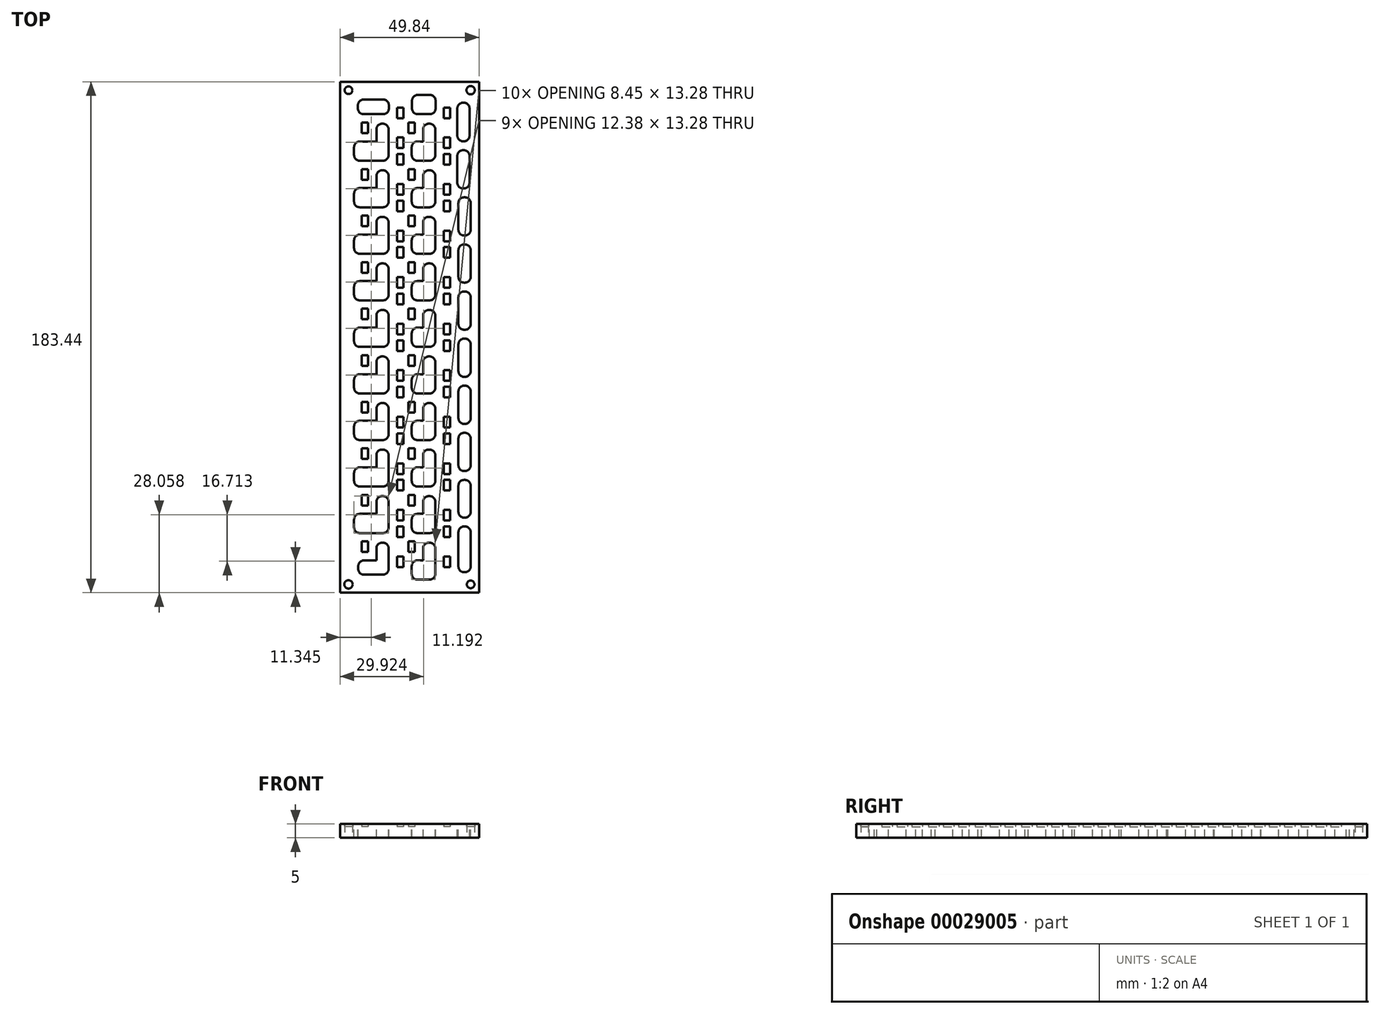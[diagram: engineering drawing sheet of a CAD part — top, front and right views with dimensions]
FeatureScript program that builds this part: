
annotation { "Feature Type Name" : "Feature", "Feature Type Description" : "" }
export const myFeature = defineFeature(function(context is Context, id is Id, definition is map)
    precondition{}
    {
        {
            var Q0;
            Q0=qCreatedBy(makeId("Top.planeOp"),FACE);
            var sketch = newSketch(context, id + "F0", { "sketchPlane" : qUnion([Q0])});
            skCircle(sketch, "E0", {"center": v(0, 0) * mm, "radius": 1.5 * mm});
            skCircle(sketch, "E1", {"center": v(43.84, 177.44) * mm, "radius": 1.5 * mm});
            skLineSegment(sketch, "E2.bottom", {"start": v(-3, 180.44) * mm, "end": v(46.84, 180.44) * mm});
            skLineSegment(sketch, "E2.top", {"start": v(-3, -3) * mm, "end": v(46.84, -3) * mm});
            skLineSegment(sketch, "E2.left", {"start": v(-3, 180.44) * mm, "end": v(-3, -3) * mm});
            skLineSegment(sketch, "E2.right", {"start": v(46.84, 180.44) * mm, "end": v(46.84, -3) * mm});
            skLineSegment(sketch, "E3.rect.bottom", {"start": v(19.7, 6.23) * mm, "end": v(17.38, 6.23) * mm});
            skLineSegment(sketch, "E3.rect.top", {"start": v(19.7, 10.04) * mm, "end": v(17.38, 10.04) * mm});
            skLineSegment(sketch, "E3.rect.left", {"start": v(19.7, 6.23) * mm, "end": v(19.7, 10.04) * mm});
            skLineSegment(sketch, "E3.rect.right", {"start": v(17.38, 6.23) * mm, "end": v(17.38, 10.04) * mm});
            skPoint(sketch, "E3.rect.middle", {"position": v(18.54, 8.14) * mm});
            skLineSegment(sketch, "E4.rect.right", {"start": v(4.72, 11.6) * mm, "end": v(4.72, 15.42) * mm});
            skLineSegment(sketch, "E4.rect.left", {"start": v(7.03, 11.6) * mm, "end": v(7.03, 15.42) * mm});
            skLineSegment(sketch, "E4.rect.top", {"start": v(7.03, 15.42) * mm, "end": v(4.72, 15.42) * mm});
            skPoint(sketch, "E4.rect.middle", {"position": v(5.88, 13.51) * mm});
            skLineSegment(sketch, "E4.rect.bottom", {"start": v(7.03, 11.6) * mm, "end": v(4.72, 11.6) * mm});
            skLineSegment(sketch, "E5.rect.top", {"start": v(19.7, 20.8) * mm, "end": v(17.38, 20.8) * mm});
            skPoint(sketch, "E5.rect.middle", {"position": v(18.54, 18.89) * mm});
            skLineSegment(sketch, "E5.rect.bottom", {"start": v(19.7, 16.98) * mm, "end": v(17.38, 16.98) * mm});
            skLineSegment(sketch, "E5.rect.left", {"start": v(19.7, 16.98) * mm, "end": v(19.7, 20.8) * mm});
            skLineSegment(sketch, "E5.rect.right", {"start": v(17.38, 16.98) * mm, "end": v(17.38, 20.8) * mm});
            skLineSegment(sketch, "E6.rect.top", {"start": v(19.7, 26.75) * mm, "end": v(17.38, 26.75) * mm});
            skLineSegment(sketch, "E7.rect.left", {"start": v(19.7, 33.7) * mm, "end": v(19.7, 37.5) * mm});
            skLineSegment(sketch, "E6.rect.bottom", {"start": v(19.7, 22.94) * mm, "end": v(17.38, 22.94) * mm});
            skPoint(sketch, "E6.rect.middle", {"position": v(18.54, 24.85) * mm});
            skLineSegment(sketch, "E8.rect.top", {"start": v(7.03, 32.13) * mm, "end": v(4.72, 32.13) * mm});
            skPoint(sketch, "E7.rect.middle", {"position": v(18.54, 35.6) * mm});
            skLineSegment(sketch, "E7.rect.bottom", {"start": v(19.7, 33.7) * mm, "end": v(17.38, 33.7) * mm});
            skLineSegment(sketch, "E7.rect.top", {"start": v(19.7, 37.5) * mm, "end": v(17.38, 37.5) * mm});
            skLineSegment(sketch, "E8.rect.bottom", {"start": v(7.03, 28.32) * mm, "end": v(4.72, 28.32) * mm});
            skLineSegment(sketch, "E7.rect.right", {"start": v(17.38, 33.7) * mm, "end": v(17.38, 37.5) * mm});
            skLineSegment(sketch, "E8.rect.left", {"start": v(7.03, 28.32) * mm, "end": v(7.03, 32.13) * mm});
            skPoint(sketch, "E8.rect.middle", {"position": v(5.88, 30.23) * mm});
            skLineSegment(sketch, "E8.rect.right", {"start": v(4.72, 28.32) * mm, "end": v(4.72, 32.13) * mm});
            skLineSegment(sketch, "E6.rect.right", {"start": v(17.38, 22.94) * mm, "end": v(17.38, 26.75) * mm});
            skLineSegment(sketch, "E6.rect.left", {"start": v(19.7, 22.94) * mm, "end": v(19.7, 26.75) * mm});
            skPoint(sketch, "E9.rect.middle", {"position": v(5.88, 46.94) * mm});
            skPoint(sketch, "E10.rect.middle", {"position": v(18.54, 52.32) * mm});
            skLineSegment(sketch, "E11.rect.left", {"start": v(19.7, 39.66) * mm, "end": v(19.7, 43.47) * mm});
            skLineSegment(sketch, "E11.rect.bottom", {"start": v(19.7, 39.66) * mm, "end": v(17.38, 39.66) * mm});
            skLineSegment(sketch, "E10.rect.top", {"start": v(19.7, 54.22) * mm, "end": v(17.38, 54.22) * mm});
            skLineSegment(sketch, "E9.rect.right", {"start": v(4.72, 45.03) * mm, "end": v(4.72, 48.84) * mm});
            skLineSegment(sketch, "E10.rect.right", {"start": v(17.38, 50.41) * mm, "end": v(17.38, 54.22) * mm});
            skLineSegment(sketch, "E9.rect.top", {"start": v(7.03, 48.84) * mm, "end": v(4.72, 48.84) * mm});
            skLineSegment(sketch, "E11.rect.right", {"start": v(17.38, 39.66) * mm, "end": v(17.38, 43.47) * mm});
            skLineSegment(sketch, "E9.rect.bottom", {"start": v(7.03, 45.03) * mm, "end": v(4.72, 45.03) * mm});
            skLineSegment(sketch, "E9.rect.left", {"start": v(7.03, 45.03) * mm, "end": v(7.03, 48.84) * mm});
            skLineSegment(sketch, "E10.rect.left", {"start": v(19.7, 50.41) * mm, "end": v(19.7, 54.22) * mm});
            skPoint(sketch, "E11.rect.middle", {"position": v(18.54, 41.56) * mm});
            skLineSegment(sketch, "E11.rect.top", {"start": v(19.7, 43.47) * mm, "end": v(17.38, 43.47) * mm});
            skLineSegment(sketch, "E10.rect.bottom", {"start": v(19.7, 50.41) * mm, "end": v(17.38, 50.41) * mm});
            skPoint(sketch, "E12.rect.middle", {"position": v(18.54, 74.99) * mm});
            skPoint(sketch, "E13.rect.middle", {"position": v(18.54, 85.74) * mm});
            skPoint(sketch, "E14.rect.middle", {"position": v(18.54, 69.03) * mm});
            skPoint(sketch, "E15.rect.middle", {"position": v(5.88, 80.37) * mm});
            skPoint(sketch, "E16.rect.middle", {"position": v(5.88, 63.65) * mm});
            skPoint(sketch, "E17.rect.middle", {"position": v(18.54, 58.28) * mm});
            skLineSegment(sketch, "E14.rect.left", {"start": v(19.7, 67.12) * mm, "end": v(19.7, 70.93) * mm});
            skLineSegment(sketch, "E12.rect.right", {"start": v(17.38, 73.08) * mm, "end": v(17.38, 76.9) * mm});
            skLineSegment(sketch, "E17.rect.left", {"start": v(19.7, 56.37) * mm, "end": v(19.7, 60.18) * mm});
            skLineSegment(sketch, "E16.rect.left", {"start": v(7.03, 61.75) * mm, "end": v(7.03, 65.56) * mm});
            skLineSegment(sketch, "E13.rect.right", {"start": v(17.38, 83.84) * mm, "end": v(17.38, 87.65) * mm});
            skLineSegment(sketch, "E15.rect.right", {"start": v(4.72, 78.46) * mm, "end": v(4.72, 82.27) * mm});
            skLineSegment(sketch, "E17.rect.right", {"start": v(17.38, 56.37) * mm, "end": v(17.38, 60.18) * mm});
            skLineSegment(sketch, "E13.rect.left", {"start": v(19.7, 83.84) * mm, "end": v(19.7, 87.65) * mm});
            skLineSegment(sketch, "E16.rect.right", {"start": v(4.72, 61.75) * mm, "end": v(4.72, 65.56) * mm});
            skLineSegment(sketch, "E15.rect.left", {"start": v(7.03, 78.46) * mm, "end": v(7.03, 82.27) * mm});
            skLineSegment(sketch, "E14.rect.right", {"start": v(17.38, 67.12) * mm, "end": v(17.38, 70.93) * mm});
            skLineSegment(sketch, "E12.rect.left", {"start": v(19.7, 73.08) * mm, "end": v(19.7, 76.9) * mm});
            skLineSegment(sketch, "E15.rect.top", {"start": v(7.03, 82.27) * mm, "end": v(4.72, 82.27) * mm});
            skLineSegment(sketch, "E17.rect.bottom", {"start": v(19.7, 56.37) * mm, "end": v(17.38, 56.37) * mm});
            skLineSegment(sketch, "E13.rect.top", {"start": v(19.7, 87.65) * mm, "end": v(17.38, 87.65) * mm});
            skLineSegment(sketch, "E17.rect.top", {"start": v(19.7, 60.18) * mm, "end": v(17.38, 60.18) * mm});
            skLineSegment(sketch, "E12.rect.bottom", {"start": v(19.7, 73.08) * mm, "end": v(17.38, 73.08) * mm});
            skLineSegment(sketch, "E13.rect.bottom", {"start": v(19.7, 83.84) * mm, "end": v(17.38, 83.84) * mm});
            skLineSegment(sketch, "E12.rect.top", {"start": v(19.7, 76.9) * mm, "end": v(17.38, 76.9) * mm});
            skLineSegment(sketch, "E14.rect.top", {"start": v(19.7, 70.93) * mm, "end": v(17.38, 70.93) * mm});
            skLineSegment(sketch, "E14.rect.bottom", {"start": v(19.7, 67.12) * mm, "end": v(17.38, 67.12) * mm});
            skLineSegment(sketch, "E15.rect.bottom", {"start": v(7.03, 78.46) * mm, "end": v(4.72, 78.46) * mm});
            skLineSegment(sketch, "E16.rect.top", {"start": v(7.03, 65.56) * mm, "end": v(4.72, 65.56) * mm});
            skLineSegment(sketch, "E16.rect.bottom", {"start": v(7.03, 61.75) * mm, "end": v(4.72, 61.75) * mm});
            skPoint(sketch, "E18.rect.middle", {"position": v(5.88, 130.5) * mm});
            skPoint(sketch, "E19.rect.middle", {"position": v(18.54, 152.6) * mm});
            skPoint(sketch, "E20.rect.middle", {"position": v(5.88, 97.08) * mm});
            skPoint(sketch, "E21.rect.middle", {"position": v(18.54, 102.46) * mm});
            skPoint(sketch, "E22.rect.middle", {"position": v(5.88, 147.22) * mm});
            skPoint(sketch, "E23.rect.middle", {"position": v(5.88, 113.8) * mm});
            skPoint(sketch, "E24.rect.middle", {"position": v(18.54, 119.17) * mm});
            skPoint(sketch, "E25.rect.middle", {"position": v(18.54, 125.13) * mm});
            skPoint(sketch, "E26.rect.middle", {"position": v(18.54, 91.7) * mm});
            skPoint(sketch, "E27.rect.middle", {"position": v(18.54, 141.84) * mm});
            skPoint(sketch, "E28.rect.middle", {"position": v(18.54, 135.88) * mm});
            skPoint(sketch, "E29.rect.middle", {"position": v(18.54, 108.42) * mm});
            skLineSegment(sketch, "E19.rect.right", {"start": v(17.38, 150.7) * mm, "end": v(17.38, 154.5) * mm});
            skLineSegment(sketch, "E23.rect.left", {"start": v(7.03, 111.89) * mm, "end": v(7.03, 115.7) * mm});
            skLineSegment(sketch, "E25.rect.left", {"start": v(19.7, 123.22) * mm, "end": v(19.7, 127.03) * mm});
            skLineSegment(sketch, "E26.rect.right", {"start": v(17.38, 89.8) * mm, "end": v(17.38, 93.6) * mm});
            skLineSegment(sketch, "E27.rect.left", {"start": v(19.7, 139.94) * mm, "end": v(19.7, 143.75) * mm});
            skLineSegment(sketch, "E18.rect.right", {"start": v(4.72, 128.6) * mm, "end": v(4.72, 132.41) * mm});
            skLineSegment(sketch, "E21.rect.right", {"start": v(17.38, 100.55) * mm, "end": v(17.38, 104.36) * mm});
            skLineSegment(sketch, "E23.rect.right", {"start": v(4.72, 111.89) * mm, "end": v(4.72, 115.7) * mm});
            skLineSegment(sketch, "E19.rect.left", {"start": v(19.7, 150.7) * mm, "end": v(19.7, 154.5) * mm});
            skLineSegment(sketch, "E25.rect.right", {"start": v(17.38, 123.22) * mm, "end": v(17.38, 127.03) * mm});
            skLineSegment(sketch, "E26.rect.left", {"start": v(19.7, 89.8) * mm, "end": v(19.7, 93.6) * mm});
            skLineSegment(sketch, "E18.rect.left", {"start": v(7.03, 128.6) * mm, "end": v(7.03, 132.41) * mm});
            skLineSegment(sketch, "E28.rect.right", {"start": v(17.38, 133.98) * mm, "end": v(17.38, 137.79) * mm});
            skLineSegment(sketch, "E20.rect.right", {"start": v(4.72, 95.17) * mm, "end": v(4.72, 98.98) * mm});
            skLineSegment(sketch, "E27.rect.right", {"start": v(17.38, 139.94) * mm, "end": v(17.38, 143.75) * mm});
            skLineSegment(sketch, "E21.rect.left", {"start": v(19.7, 100.55) * mm, "end": v(19.7, 104.36) * mm});
            skLineSegment(sketch, "E28.rect.left", {"start": v(19.7, 133.98) * mm, "end": v(19.7, 137.79) * mm});
            skLineSegment(sketch, "E20.rect.left", {"start": v(7.03, 95.17) * mm, "end": v(7.03, 98.98) * mm});
            skLineSegment(sketch, "E24.rect.left", {"start": v(19.7, 117.26) * mm, "end": v(19.7, 121.07) * mm});
            skLineSegment(sketch, "E25.rect.bottom", {"start": v(19.7, 123.22) * mm, "end": v(17.38, 123.22) * mm});
            skLineSegment(sketch, "E21.rect.top", {"start": v(19.7, 104.36) * mm, "end": v(17.38, 104.36) * mm});
            skLineSegment(sketch, "E23.rect.bottom", {"start": v(7.03, 111.89) * mm, "end": v(4.72, 111.89) * mm});
            skLineSegment(sketch, "E22.rect.right", {"start": v(4.72, 145.31) * mm, "end": v(4.72, 149.12) * mm});
            skLineSegment(sketch, "E29.rect.top", {"start": v(19.7, 110.32) * mm, "end": v(17.38, 110.32) * mm});
            skLineSegment(sketch, "E22.rect.bottom", {"start": v(7.03, 145.31) * mm, "end": v(4.72, 145.31) * mm});
            skLineSegment(sketch, "E29.rect.left", {"start": v(19.7, 106.51) * mm, "end": v(19.7, 110.32) * mm});
            skLineSegment(sketch, "E29.rect.bottom", {"start": v(19.7, 106.51) * mm, "end": v(17.38, 106.51) * mm});
            skLineSegment(sketch, "E18.rect.bottom", {"start": v(7.03, 128.6) * mm, "end": v(4.72, 128.6) * mm});
            skLineSegment(sketch, "E21.rect.bottom", {"start": v(19.7, 100.55) * mm, "end": v(17.38, 100.55) * mm});
            skLineSegment(sketch, "E20.rect.top", {"start": v(7.03, 98.98) * mm, "end": v(4.72, 98.98) * mm});
            skLineSegment(sketch, "E28.rect.bottom", {"start": v(19.7, 133.98) * mm, "end": v(17.38, 133.98) * mm});
            skLineSegment(sketch, "E24.rect.right", {"start": v(17.38, 117.26) * mm, "end": v(17.38, 121.07) * mm});
            skLineSegment(sketch, "E26.rect.top", {"start": v(19.7, 93.6) * mm, "end": v(17.38, 93.6) * mm});
            skLineSegment(sketch, "E24.rect.bottom", {"start": v(19.7, 117.26) * mm, "end": v(17.38, 117.26) * mm});
            skLineSegment(sketch, "E20.rect.bottom", {"start": v(7.03, 95.17) * mm, "end": v(4.72, 95.17) * mm});
            skLineSegment(sketch, "E19.rect.top", {"start": v(19.7, 154.5) * mm, "end": v(17.38, 154.5) * mm});
            skLineSegment(sketch, "E22.rect.top", {"start": v(7.03, 149.12) * mm, "end": v(4.72, 149.12) * mm});
            skLineSegment(sketch, "E24.rect.top", {"start": v(19.7, 121.07) * mm, "end": v(17.38, 121.07) * mm});
            skLineSegment(sketch, "E18.rect.top", {"start": v(7.03, 132.41) * mm, "end": v(4.72, 132.41) * mm});
            skLineSegment(sketch, "E28.rect.top", {"start": v(19.7, 137.79) * mm, "end": v(17.38, 137.79) * mm});
            skLineSegment(sketch, "E26.rect.bottom", {"start": v(19.7, 89.8) * mm, "end": v(17.38, 89.8) * mm});
            skLineSegment(sketch, "E19.rect.bottom", {"start": v(19.7, 150.7) * mm, "end": v(17.38, 150.7) * mm});
            skLineSegment(sketch, "E23.rect.top", {"start": v(7.03, 115.7) * mm, "end": v(4.72, 115.7) * mm});
            skLineSegment(sketch, "E22.rect.left", {"start": v(7.03, 145.31) * mm, "end": v(7.03, 149.12) * mm});
            skLineSegment(sketch, "E27.rect.bottom", {"start": v(19.7, 139.94) * mm, "end": v(17.38, 139.94) * mm});
            skLineSegment(sketch, "E27.rect.top", {"start": v(19.7, 143.75) * mm, "end": v(17.38, 143.75) * mm});
            skLineSegment(sketch, "E25.rect.top", {"start": v(19.7, 127.03) * mm, "end": v(17.38, 127.03) * mm});
            skLineSegment(sketch, "E29.rect.right", {"start": v(17.38, 106.51) * mm, "end": v(17.38, 110.32) * mm});
            skPoint(sketch, "E30.rect.middle", {"position": v(18.54, 169.3) * mm});
            skPoint(sketch, "E31.rect.middle", {"position": v(18.54, 158.56) * mm});
            skPoint(sketch, "E32.rect.middle", {"position": v(5.88, 163.93) * mm});
            skLineSegment(sketch, "E32.rect.left", {"start": v(7.03, 162.03) * mm, "end": v(7.03, 165.84) * mm});
            skLineSegment(sketch, "E31.rect.right", {"start": v(17.38, 156.65) * mm, "end": v(17.38, 160.46) * mm});
            skLineSegment(sketch, "E30.rect.right", {"start": v(17.38, 167.4) * mm, "end": v(17.38, 171.21) * mm});
            skLineSegment(sketch, "E30.rect.left", {"start": v(19.7, 167.4) * mm, "end": v(19.7, 171.21) * mm});
            skLineSegment(sketch, "E32.rect.right", {"start": v(4.72, 162.03) * mm, "end": v(4.72, 165.84) * mm});
            skLineSegment(sketch, "E31.rect.left", {"start": v(19.7, 156.65) * mm, "end": v(19.7, 160.46) * mm});
            skLineSegment(sketch, "E30.rect.bottom", {"start": v(19.7, 167.4) * mm, "end": v(17.38, 167.4) * mm});
            skLineSegment(sketch, "E31.rect.top", {"start": v(19.7, 160.46) * mm, "end": v(17.38, 160.46) * mm});
            skLineSegment(sketch, "E31.rect.bottom", {"start": v(19.7, 156.65) * mm, "end": v(17.38, 156.65) * mm});
            skLineSegment(sketch, "E32.rect.bottom", {"start": v(7.03, 162.03) * mm, "end": v(4.72, 162.03) * mm});
            skLineSegment(sketch, "E32.rect.top", {"start": v(7.03, 165.84) * mm, "end": v(4.72, 165.84) * mm});
            skLineSegment(sketch, "E30.rect.top", {"start": v(19.7, 171.21) * mm, "end": v(17.38, 171.21) * mm});
            skPoint(sketch, "E33.rect.middle", {"position": v(35.3, 135.88) * mm});
            skPoint(sketch, "E34.rect.middle", {"position": v(35.3, 74.99) * mm});
            skPoint(sketch, "E35.rect.middle", {"position": v(22.64, 63.65) * mm});
            skPoint(sketch, "E36.rect.middle", {"position": v(22.64, 97.08) * mm});
            skPoint(sketch, "E37.rect.middle", {"position": v(35.3, 8.14) * mm});
            skPoint(sketch, "E38.rect.middle", {"position": v(35.3, 35.6) * mm});
            skPoint(sketch, "E39.rect.middle", {"position": v(35.3, 108.42) * mm});
            skPoint(sketch, "E40.rect.middle", {"position": v(35.3, 58.28) * mm});
            skPoint(sketch, "E41.rect.middle", {"position": v(35.3, 158.56) * mm});
            skPoint(sketch, "E42.rect.middle", {"position": v(35.3, 24.85) * mm});
            skPoint(sketch, "E43.rect.middle", {"position": v(22.64, 130.5) * mm});
            skPoint(sketch, "E44.rect.middle", {"position": v(35.3, 18.89) * mm});
            skPoint(sketch, "E45.rect.middle", {"position": v(35.3, 102.46) * mm});
            skPoint(sketch, "E46.rect.middle", {"position": v(35.3, 125.13) * mm});
            skPoint(sketch, "E47.rect.middle", {"position": v(35.3, 91.7) * mm});
            skPoint(sketch, "E48.rect.middle", {"position": v(35.3, 41.56) * mm});
            skPoint(sketch, "E49.rect.middle", {"position": v(35.3, 141.84) * mm});
            skPoint(sketch, "E50.rect.middle", {"position": v(35.3, 85.74) * mm});
            skPoint(sketch, "E51.rect.middle", {"position": v(35.3, 69.03) * mm});
            skPoint(sketch, "E52.rect.middle", {"position": v(35.3, 169.3) * mm});
            skPoint(sketch, "E53.rect.middle", {"position": v(35.3, 152.6) * mm});
            skPoint(sketch, "E54.rect.middle", {"position": v(22.64, 163.93) * mm});
            skPoint(sketch, "E55.rect.middle", {"position": v(22.64, 13.51) * mm});
            skPoint(sketch, "E56.rect.middle", {"position": v(22.64, 113.8) * mm});
            skPoint(sketch, "E57.rect.middle", {"position": v(22.64, 147.22) * mm});
            skPoint(sketch, "E58.rect.middle", {"position": v(22.64, 80.37) * mm});
            skPoint(sketch, "E59.rect.middle", {"position": v(35.3, 119.17) * mm});
            skPoint(sketch, "E60.rect.middle", {"position": v(22.64, 30.23) * mm});
            skPoint(sketch, "E61.rect.middle", {"position": v(22.64, 46.94) * mm});
            skPoint(sketch, "E62.rect.middle", {"position": v(35.3, 52.32) * mm});
            skLineSegment(sketch, "E52.rect.top", {"start": v(36.46, 171.21) * mm, "end": v(34.15, 171.21) * mm});
            skLineSegment(sketch, "E37.rect.bottom", {"start": v(36.46, 6.23) * mm, "end": v(34.15, 6.23) * mm});
            skLineSegment(sketch, "E47.rect.top", {"start": v(36.46, 93.6) * mm, "end": v(34.15, 93.6) * mm});
            skLineSegment(sketch, "E57.rect.bottom", {"start": v(23.8, 145.31) * mm, "end": v(21.48, 145.31) * mm});
            skLineSegment(sketch, "E35.rect.left", {"start": v(23.8, 61.75) * mm, "end": v(23.8, 65.56) * mm});
            skLineSegment(sketch, "E53.rect.bottom", {"start": v(36.46, 150.7) * mm, "end": v(34.15, 150.7) * mm});
            skLineSegment(sketch, "E52.rect.left", {"start": v(36.46, 167.4) * mm, "end": v(36.46, 171.21) * mm});
            skLineSegment(sketch, "E34.rect.left", {"start": v(36.46, 73.08) * mm, "end": v(36.46, 76.9) * mm});
            skLineSegment(sketch, "E34.rect.top", {"start": v(36.46, 76.9) * mm, "end": v(34.15, 76.9) * mm});
            skLineSegment(sketch, "E45.rect.bottom", {"start": v(36.46, 100.55) * mm, "end": v(34.15, 100.55) * mm});
            skLineSegment(sketch, "E52.rect.bottom", {"start": v(36.46, 167.4) * mm, "end": v(34.15, 167.4) * mm});
            skLineSegment(sketch, "E48.rect.top", {"start": v(36.46, 43.47) * mm, "end": v(34.15, 43.47) * mm});
            skLineSegment(sketch, "E43.rect.bottom", {"start": v(23.8, 128.6) * mm, "end": v(21.48, 128.6) * mm});
            skLineSegment(sketch, "E47.rect.right", {"start": v(34.15, 89.8) * mm, "end": v(34.15, 93.6) * mm});
            skLineSegment(sketch, "E58.rect.top", {"start": v(23.8, 82.27) * mm, "end": v(21.48, 82.27) * mm});
            skLineSegment(sketch, "E34.rect.right", {"start": v(34.15, 73.08) * mm, "end": v(34.15, 76.9) * mm});
            skLineSegment(sketch, "E50.rect.bottom", {"start": v(36.46, 83.84) * mm, "end": v(34.15, 83.84) * mm});
            skLineSegment(sketch, "E38.rect.bottom", {"start": v(36.46, 33.7) * mm, "end": v(34.15, 33.7) * mm});
            skLineSegment(sketch, "E44.rect.bottom", {"start": v(36.46, 16.98) * mm, "end": v(34.15, 16.98) * mm});
            skLineSegment(sketch, "E55.rect.bottom", {"start": v(23.8, 11.6) * mm, "end": v(21.48, 11.6) * mm});
            skLineSegment(sketch, "E36.rect.top", {"start": v(23.8, 98.98) * mm, "end": v(21.48, 98.98) * mm});
            skLineSegment(sketch, "E49.rect.top", {"start": v(36.46, 143.75) * mm, "end": v(34.15, 143.75) * mm});
            skLineSegment(sketch, "E39.rect.top", {"start": v(36.46, 110.32) * mm, "end": v(34.15, 110.32) * mm});
            skLineSegment(sketch, "E41.rect.top", {"start": v(36.46, 160.46) * mm, "end": v(34.15, 160.46) * mm});
            skLineSegment(sketch, "E62.rect.bottom", {"start": v(36.46, 50.41) * mm, "end": v(34.15, 50.41) * mm});
            skLineSegment(sketch, "E40.rect.top", {"start": v(36.46, 60.18) * mm, "end": v(34.15, 60.18) * mm});
            skLineSegment(sketch, "E51.rect.bottom", {"start": v(36.46, 67.12) * mm, "end": v(34.15, 67.12) * mm});
            skLineSegment(sketch, "E33.rect.right", {"start": v(34.15, 133.98) * mm, "end": v(34.15, 137.79) * mm});
            skLineSegment(sketch, "E47.rect.left", {"start": v(36.46, 89.8) * mm, "end": v(36.46, 93.6) * mm});
            skLineSegment(sketch, "E37.rect.top", {"start": v(36.46, 10.04) * mm, "end": v(34.15, 10.04) * mm});
            skLineSegment(sketch, "E37.rect.left", {"start": v(36.46, 6.23) * mm, "end": v(36.46, 10.04) * mm});
            skLineSegment(sketch, "E37.rect.right", {"start": v(34.15, 6.23) * mm, "end": v(34.15, 10.04) * mm});
            skLineSegment(sketch, "E46.rect.top", {"start": v(36.46, 127.03) * mm, "end": v(34.15, 127.03) * mm});
            skLineSegment(sketch, "E33.rect.bottom", {"start": v(36.46, 133.98) * mm, "end": v(34.15, 133.98) * mm});
            skLineSegment(sketch, "E44.rect.left", {"start": v(36.46, 16.98) * mm, "end": v(36.46, 20.8) * mm});
            skLineSegment(sketch, "E35.rect.top", {"start": v(23.8, 65.56) * mm, "end": v(21.48, 65.56) * mm});
            skLineSegment(sketch, "E44.rect.right", {"start": v(34.15, 16.98) * mm, "end": v(34.15, 20.8) * mm});
            skLineSegment(sketch, "E35.rect.bottom", {"start": v(23.8, 61.75) * mm, "end": v(21.48, 61.75) * mm});
            skLineSegment(sketch, "E42.rect.top", {"start": v(36.46, 26.75) * mm, "end": v(34.15, 26.75) * mm});
            skLineSegment(sketch, "E33.rect.left", {"start": v(36.46, 133.98) * mm, "end": v(36.46, 137.79) * mm});
            skLineSegment(sketch, "E35.rect.right", {"start": v(21.48, 61.75) * mm, "end": v(21.48, 65.56) * mm});
            skLineSegment(sketch, "E52.rect.right", {"start": v(34.15, 167.4) * mm, "end": v(34.15, 171.21) * mm});
            skLineSegment(sketch, "E62.rect.left", {"start": v(36.46, 50.41) * mm, "end": v(36.46, 54.22) * mm});
            skLineSegment(sketch, "E38.rect.top", {"start": v(36.46, 37.5) * mm, "end": v(34.15, 37.5) * mm});
            skLineSegment(sketch, "E41.rect.left", {"start": v(36.46, 156.65) * mm, "end": v(36.46, 160.46) * mm});
            skLineSegment(sketch, "E51.rect.top", {"start": v(36.46, 70.93) * mm, "end": v(34.15, 70.93) * mm});
            skLineSegment(sketch, "E59.rect.top", {"start": v(36.46, 121.07) * mm, "end": v(34.15, 121.07) * mm});
            skLineSegment(sketch, "E40.rect.bottom", {"start": v(36.46, 56.37) * mm, "end": v(34.15, 56.37) * mm});
            skLineSegment(sketch, "E43.rect.right", {"start": v(21.48, 128.6) * mm, "end": v(21.48, 132.41) * mm});
            skLineSegment(sketch, "E56.rect.bottom", {"start": v(23.8, 111.89) * mm, "end": v(21.48, 111.89) * mm});
            skLineSegment(sketch, "E53.rect.left", {"start": v(36.46, 150.7) * mm, "end": v(36.46, 154.5) * mm});
            skLineSegment(sketch, "E39.rect.left", {"start": v(36.46, 106.51) * mm, "end": v(36.46, 110.32) * mm});
            skLineSegment(sketch, "E47.rect.bottom", {"start": v(36.46, 89.8) * mm, "end": v(34.15, 89.8) * mm});
            skLineSegment(sketch, "E46.rect.right", {"start": v(34.15, 123.22) * mm, "end": v(34.15, 127.03) * mm});
            skLineSegment(sketch, "E41.rect.bottom", {"start": v(36.46, 156.65) * mm, "end": v(34.15, 156.65) * mm});
            skLineSegment(sketch, "E43.rect.left", {"start": v(23.8, 128.6) * mm, "end": v(23.8, 132.41) * mm});
            skLineSegment(sketch, "E57.rect.right", {"start": v(21.48, 145.31) * mm, "end": v(21.48, 149.12) * mm});
            skLineSegment(sketch, "E53.rect.top", {"start": v(36.46, 154.5) * mm, "end": v(34.15, 154.5) * mm});
            skLineSegment(sketch, "E56.rect.top", {"start": v(23.8, 115.7) * mm, "end": v(21.48, 115.7) * mm});
            skLineSegment(sketch, "E61.rect.bottom", {"start": v(23.8, 45.03) * mm, "end": v(21.48, 45.03) * mm});
            skLineSegment(sketch, "E40.rect.left", {"start": v(36.46, 56.37) * mm, "end": v(36.46, 60.18) * mm});
            skLineSegment(sketch, "E50.rect.top", {"start": v(36.46, 87.65) * mm, "end": v(34.15, 87.65) * mm});
            skLineSegment(sketch, "E46.rect.bottom", {"start": v(36.46, 123.22) * mm, "end": v(34.15, 123.22) * mm});
            skLineSegment(sketch, "E43.rect.top", {"start": v(23.8, 132.41) * mm, "end": v(21.48, 132.41) * mm});
            skLineSegment(sketch, "E57.rect.left", {"start": v(23.8, 145.31) * mm, "end": v(23.8, 149.12) * mm});
            skLineSegment(sketch, "E57.rect.top", {"start": v(23.8, 149.12) * mm, "end": v(21.48, 149.12) * mm});
            skLineSegment(sketch, "E61.rect.left", {"start": v(23.8, 45.03) * mm, "end": v(23.8, 48.84) * mm});
            skLineSegment(sketch, "E45.rect.top", {"start": v(36.46, 104.36) * mm, "end": v(34.15, 104.36) * mm});
            skLineSegment(sketch, "E51.rect.left", {"start": v(36.46, 67.12) * mm, "end": v(36.46, 70.93) * mm});
            skLineSegment(sketch, "E34.rect.bottom", {"start": v(36.46, 73.08) * mm, "end": v(34.15, 73.08) * mm});
            skLineSegment(sketch, "E48.rect.bottom", {"start": v(36.46, 39.66) * mm, "end": v(34.15, 39.66) * mm});
            skLineSegment(sketch, "E36.rect.right", {"start": v(21.48, 95.17) * mm, "end": v(21.48, 98.98) * mm});
            skLineSegment(sketch, "E56.rect.right", {"start": v(21.48, 111.89) * mm, "end": v(21.48, 115.7) * mm});
            skLineSegment(sketch, "E38.rect.right", {"start": v(34.15, 33.7) * mm, "end": v(34.15, 37.5) * mm});
            skLineSegment(sketch, "E48.rect.left", {"start": v(36.46, 39.66) * mm, "end": v(36.46, 43.47) * mm});
            skLineSegment(sketch, "E50.rect.right", {"start": v(34.15, 83.84) * mm, "end": v(34.15, 87.65) * mm});
            skLineSegment(sketch, "E45.rect.right", {"start": v(34.15, 100.55) * mm, "end": v(34.15, 104.36) * mm});
            skLineSegment(sketch, "E39.rect.bottom", {"start": v(36.46, 106.51) * mm, "end": v(34.15, 106.51) * mm});
            skLineSegment(sketch, "E55.rect.right", {"start": v(21.48, 11.6) * mm, "end": v(21.48, 15.42) * mm});
            skLineSegment(sketch, "E55.rect.left", {"start": v(23.8, 11.6) * mm, "end": v(23.8, 15.42) * mm});
            skLineSegment(sketch, "E55.rect.top", {"start": v(23.8, 15.42) * mm, "end": v(21.48, 15.42) * mm});
            skLineSegment(sketch, "E40.rect.right", {"start": v(34.15, 56.37) * mm, "end": v(34.15, 60.18) * mm});
            skLineSegment(sketch, "E62.rect.top", {"start": v(36.46, 54.22) * mm, "end": v(34.15, 54.22) * mm});
            skLineSegment(sketch, "E45.rect.left", {"start": v(36.46, 100.55) * mm, "end": v(36.46, 104.36) * mm});
            skLineSegment(sketch, "E50.rect.left", {"start": v(36.46, 83.84) * mm, "end": v(36.46, 87.65) * mm});
            skLineSegment(sketch, "E61.rect.right", {"start": v(21.48, 45.03) * mm, "end": v(21.48, 48.84) * mm});
            skLineSegment(sketch, "E39.rect.right", {"start": v(34.15, 106.51) * mm, "end": v(34.15, 110.32) * mm});
            skLineSegment(sketch, "E59.rect.right", {"start": v(34.15, 117.26) * mm, "end": v(34.15, 121.07) * mm});
            skLineSegment(sketch, "E53.rect.right", {"start": v(34.15, 150.7) * mm, "end": v(34.15, 154.5) * mm});
            skLineSegment(sketch, "E38.rect.left", {"start": v(36.46, 33.7) * mm, "end": v(36.46, 37.5) * mm});
            skLineSegment(sketch, "E36.rect.left", {"start": v(23.8, 95.17) * mm, "end": v(23.8, 98.98) * mm});
            skLineSegment(sketch, "E56.rect.left", {"start": v(23.8, 111.89) * mm, "end": v(23.8, 115.7) * mm});
            skLineSegment(sketch, "E61.rect.top", {"start": v(23.8, 48.84) * mm, "end": v(21.48, 48.84) * mm});
            skLineSegment(sketch, "E41.rect.right", {"start": v(34.15, 156.65) * mm, "end": v(34.15, 160.46) * mm});
            skLineSegment(sketch, "E59.rect.bottom", {"start": v(36.46, 117.26) * mm, "end": v(34.15, 117.26) * mm});
            skLineSegment(sketch, "E59.rect.left", {"start": v(36.46, 117.26) * mm, "end": v(36.46, 121.07) * mm});
            skLineSegment(sketch, "E46.rect.left", {"start": v(36.46, 123.22) * mm, "end": v(36.46, 127.03) * mm});
            skLineSegment(sketch, "E51.rect.right", {"start": v(34.15, 67.12) * mm, "end": v(34.15, 70.93) * mm});
            skLineSegment(sketch, "E48.rect.right", {"start": v(34.15, 39.66) * mm, "end": v(34.15, 43.47) * mm});
            skLineSegment(sketch, "E36.rect.bottom", {"start": v(23.8, 95.17) * mm, "end": v(21.48, 95.17) * mm});
            skLineSegment(sketch, "E60.rect.top", {"start": v(23.8, 32.13) * mm, "end": v(21.48, 32.13) * mm});
            skLineSegment(sketch, "E62.rect.right", {"start": v(34.15, 50.41) * mm, "end": v(34.15, 54.22) * mm});
            skLineSegment(sketch, "E42.rect.left", {"start": v(36.46, 22.94) * mm, "end": v(36.46, 26.75) * mm});
            skLineSegment(sketch, "E54.rect.bottom", {"start": v(23.8, 162.03) * mm, "end": v(21.48, 162.03) * mm});
            skLineSegment(sketch, "E60.rect.left", {"start": v(23.8, 28.32) * mm, "end": v(23.8, 32.13) * mm});
            skLineSegment(sketch, "E54.rect.top", {"start": v(23.8, 165.84) * mm, "end": v(21.48, 165.84) * mm});
            skLineSegment(sketch, "E60.rect.bottom", {"start": v(23.8, 28.32) * mm, "end": v(21.48, 28.32) * mm});
            skLineSegment(sketch, "E42.rect.right", {"start": v(34.15, 22.94) * mm, "end": v(34.15, 26.75) * mm});
            skLineSegment(sketch, "E60.rect.right", {"start": v(21.48, 28.32) * mm, "end": v(21.48, 32.13) * mm});
            skLineSegment(sketch, "E54.rect.right", {"start": v(21.48, 162.03) * mm, "end": v(21.48, 165.84) * mm});
            skLineSegment(sketch, "E49.rect.left", {"start": v(36.46, 139.94) * mm, "end": v(36.46, 143.75) * mm});
            skLineSegment(sketch, "E44.rect.top", {"start": v(36.46, 20.8) * mm, "end": v(34.15, 20.8) * mm});
            skLineSegment(sketch, "E58.rect.right", {"start": v(21.48, 78.46) * mm, "end": v(21.48, 82.27) * mm});
            skLineSegment(sketch, "E58.rect.bottom", {"start": v(23.8, 78.46) * mm, "end": v(21.48, 78.46) * mm});
            skLineSegment(sketch, "E33.rect.top", {"start": v(36.46, 137.79) * mm, "end": v(34.15, 137.79) * mm});
            skLineSegment(sketch, "E49.rect.bottom", {"start": v(36.46, 139.94) * mm, "end": v(34.15, 139.94) * mm});
            skLineSegment(sketch, "E49.rect.right", {"start": v(34.15, 139.94) * mm, "end": v(34.15, 143.75) * mm});
            skLineSegment(sketch, "E58.rect.left", {"start": v(23.8, 78.46) * mm, "end": v(23.8, 82.27) * mm});
            skLineSegment(sketch, "E54.rect.left", {"start": v(23.8, 162.03) * mm, "end": v(23.8, 165.84) * mm});
            skLineSegment(sketch, "E42.rect.bottom", {"start": v(36.46, 22.94) * mm, "end": v(34.15, 22.94) * mm});
            skCircle(sketch, "E63", {"center": v(0, 177.44) * mm, "radius": 1.38 * mm});
            skCircle(sketch, "E64", {"center": v(43.84, 0) * mm, "radius": 1.38 * mm});
            skSolve(sketch);
        }
        {
            var Q0;
            Q0=makeQuery(id+"F0.imprint","IMPRINT",FACE,{"disambiguationData":[TD([[makeQuery(id+"F0.imprint","IMPRINT",EDGE,{"derivedFrom":sQuery(id+"F0.wireOp",EDGE,"E0")}),-1.0]])]});
            extrude(context, id + "F1", {"entities" : qUnion([Q0]), "depth" : 1 * mm});
        }
        {
            var Q0;
            Q0=makeQuery(id+"F1.opExtrude","CAP_FACE",FACE,{"disambiguationData":[OSD([sQuery(id+"F0.wireOp",EDGE,"E0"),sQuery(id+"F0.wireOp",EDGE,"E1"),sQuery(id+"F0.wireOp",EDGE,"E2.bottom"),sQuery(id+"F0.wireOp",EDGE,"E2.top"),sQuery(id+"F0.wireOp",EDGE,"E2.left"),sQuery(id+"F0.wireOp",EDGE,"E2.right"),sQuery(id+"F0.wireOp",EDGE,"E3.rect.bottom"),sQuery(id+"F0.wireOp",EDGE,"E3.rect.top"),sQuery(id+"F0.wireOp",EDGE,"E3.rect.left"),sQuery(id+"F0.wireOp",EDGE,"E3.rect.right"),sQuery(id+"F0.wireOp",EDGE,"E4.rect.right"),sQuery(id+"F0.wireOp",EDGE,"E4.rect.left"),sQuery(id+"F0.wireOp",EDGE,"E4.rect.top"),sQuery(id+"F0.wireOp",EDGE,"E4.rect.bottom"),sQuery(id+"F0.wireOp",EDGE,"E5.rect.top"),sQuery(id+"F0.wireOp",EDGE,"E5.rect.bottom"),sQuery(id+"F0.wireOp",EDGE,"E5.rect.left"),sQuery(id+"F0.wireOp",EDGE,"E5.rect.right"),sQuery(id+"F0.wireOp",EDGE,"E6.rect.top"),sQuery(id+"F0.wireOp",EDGE,"E7.rect.left"),sQuery(id+"F0.wireOp",EDGE,"E6.rect.bottom"),sQuery(id+"F0.wireOp",EDGE,"E8.rect.top"),sQuery(id+"F0.wireOp",EDGE,"E7.rect.bottom"),sQuery(id+"F0.wireOp",EDGE,"E7.rect.top"),sQuery(id+"F0.wireOp",EDGE,"E8.rect.bottom"),sQuery(id+"F0.wireOp",EDGE,"E7.rect.right"),sQuery(id+"F0.wireOp",EDGE,"E8.rect.left"),sQuery(id+"F0.wireOp",EDGE,"E8.rect.right"),sQuery(id+"F0.wireOp",EDGE,"E6.rect.right"),sQuery(id+"F0.wireOp",EDGE,"E6.rect.left"),sQuery(id+"F0.wireOp",EDGE,"E11.rect.left"),sQuery(id+"F0.wireOp",EDGE,"E11.rect.bottom"),sQuery(id+"F0.wireOp",EDGE,"E10.rect.top"),sQuery(id+"F0.wireOp",EDGE,"E9.rect.right"),sQuery(id+"F0.wireOp",EDGE,"E10.rect.right"),sQuery(id+"F0.wireOp",EDGE,"E9.rect.top"),sQuery(id+"F0.wireOp",EDGE,"E11.rect.right"),sQuery(id+"F0.wireOp",EDGE,"E9.rect.bottom"),sQuery(id+"F0.wireOp",EDGE,"E9.rect.left"),sQuery(id+"F0.wireOp",EDGE,"E10.rect.left"),sQuery(id+"F0.wireOp",EDGE,"E11.rect.top"),sQuery(id+"F0.wireOp",EDGE,"E10.rect.bottom"),sQuery(id+"F0.wireOp",EDGE,"E14.rect.left"),sQuery(id+"F0.wireOp",EDGE,"E12.rect.right"),sQuery(id+"F0.wireOp",EDGE,"E17.rect.left"),sQuery(id+"F0.wireOp",EDGE,"E16.rect.left"),sQuery(id+"F0.wireOp",EDGE,"E13.rect.right"),sQuery(id+"F0.wireOp",EDGE,"E15.rect.right"),sQuery(id+"F0.wireOp",EDGE,"E17.rect.right"),sQuery(id+"F0.wireOp",EDGE,"E13.rect.left"),sQuery(id+"F0.wireOp",EDGE,"E16.rect.right"),sQuery(id+"F0.wireOp",EDGE,"E15.rect.left"),sQuery(id+"F0.wireOp",EDGE,"E14.rect.right"),sQuery(id+"F0.wireOp",EDGE,"E12.rect.left"),sQuery(id+"F0.wireOp",EDGE,"E15.rect.top"),sQuery(id+"F0.wireOp",EDGE,"E17.rect.bottom"),sQuery(id+"F0.wireOp",EDGE,"E13.rect.top"),sQuery(id+"F0.wireOp",EDGE,"E17.rect.top"),sQuery(id+"F0.wireOp",EDGE,"E12.rect.bottom"),sQuery(id+"F0.wireOp",EDGE,"E13.rect.bottom"),sQuery(id+"F0.wireOp",EDGE,"E12.rect.top"),sQuery(id+"F0.wireOp",EDGE,"E14.rect.top"),sQuery(id+"F0.wireOp",EDGE,"E14.rect.bottom"),sQuery(id+"F0.wireOp",EDGE,"E15.rect.bottom"),sQuery(id+"F0.wireOp",EDGE,"E16.rect.top"),sQuery(id+"F0.wireOp",EDGE,"E16.rect.bottom"),sQuery(id+"F0.wireOp",EDGE,"E19.rect.right"),sQuery(id+"F0.wireOp",EDGE,"E23.rect.left"),sQuery(id+"F0.wireOp",EDGE,"E25.rect.left"),sQuery(id+"F0.wireOp",EDGE,"E26.rect.right"),sQuery(id+"F0.wireOp",EDGE,"E27.rect.left"),sQuery(id+"F0.wireOp",EDGE,"E18.rect.right"),sQuery(id+"F0.wireOp",EDGE,"E21.rect.right"),sQuery(id+"F0.wireOp",EDGE,"E23.rect.right"),sQuery(id+"F0.wireOp",EDGE,"E19.rect.left"),sQuery(id+"F0.wireOp",EDGE,"E25.rect.right"),sQuery(id+"F0.wireOp",EDGE,"E26.rect.left"),sQuery(id+"F0.wireOp",EDGE,"E18.rect.left"),sQuery(id+"F0.wireOp",EDGE,"E28.rect.right"),sQuery(id+"F0.wireOp",EDGE,"E20.rect.right"),sQuery(id+"F0.wireOp",EDGE,"E27.rect.right"),sQuery(id+"F0.wireOp",EDGE,"E21.rect.left"),sQuery(id+"F0.wireOp",EDGE,"E28.rect.left"),sQuery(id+"F0.wireOp",EDGE,"E20.rect.left"),sQuery(id+"F0.wireOp",EDGE,"E24.rect.left"),sQuery(id+"F0.wireOp",EDGE,"E25.rect.bottom"),sQuery(id+"F0.wireOp",EDGE,"E21.rect.top"),sQuery(id+"F0.wireOp",EDGE,"E23.rect.bottom"),sQuery(id+"F0.wireOp",EDGE,"E22.rect.right"),sQuery(id+"F0.wireOp",EDGE,"E29.rect.top"),sQuery(id+"F0.wireOp",EDGE,"E22.rect.bottom"),sQuery(id+"F0.wireOp",EDGE,"E29.rect.left"),sQuery(id+"F0.wireOp",EDGE,"E29.rect.bottom"),sQuery(id+"F0.wireOp",EDGE,"E18.rect.bottom"),sQuery(id+"F0.wireOp",EDGE,"E21.rect.bottom"),sQuery(id+"F0.wireOp",EDGE,"E20.rect.top"),sQuery(id+"F0.wireOp",EDGE,"E28.rect.bottom"),sQuery(id+"F0.wireOp",EDGE,"E24.rect.right"),sQuery(id+"F0.wireOp",EDGE,"E26.rect.top"),sQuery(id+"F0.wireOp",EDGE,"E24.rect.bottom"),sQuery(id+"F0.wireOp",EDGE,"E20.rect.bottom"),sQuery(id+"F0.wireOp",EDGE,"E19.rect.top"),sQuery(id+"F0.wireOp",EDGE,"E22.rect.top"),sQuery(id+"F0.wireOp",EDGE,"E24.rect.top"),sQuery(id+"F0.wireOp",EDGE,"E18.rect.top"),sQuery(id+"F0.wireOp",EDGE,"E28.rect.top"),sQuery(id+"F0.wireOp",EDGE,"E26.rect.bottom"),sQuery(id+"F0.wireOp",EDGE,"E19.rect.bottom"),sQuery(id+"F0.wireOp",EDGE,"E23.rect.top"),sQuery(id+"F0.wireOp",EDGE,"E22.rect.left"),sQuery(id+"F0.wireOp",EDGE,"E27.rect.bottom"),sQuery(id+"F0.wireOp",EDGE,"E27.rect.top"),sQuery(id+"F0.wireOp",EDGE,"E25.rect.top"),sQuery(id+"F0.wireOp",EDGE,"E29.rect.right"),sQuery(id+"F0.wireOp",EDGE,"E32.rect.left"),sQuery(id+"F0.wireOp",EDGE,"E31.rect.right"),sQuery(id+"F0.wireOp",EDGE,"E30.rect.right"),sQuery(id+"F0.wireOp",EDGE,"E30.rect.left"),sQuery(id+"F0.wireOp",EDGE,"E32.rect.right"),sQuery(id+"F0.wireOp",EDGE,"E31.rect.left"),sQuery(id+"F0.wireOp",EDGE,"E30.rect.bottom"),sQuery(id+"F0.wireOp",EDGE,"E31.rect.top"),sQuery(id+"F0.wireOp",EDGE,"E31.rect.bottom"),sQuery(id+"F0.wireOp",EDGE,"E32.rect.bottom"),sQuery(id+"F0.wireOp",EDGE,"E32.rect.top"),sQuery(id+"F0.wireOp",EDGE,"E30.rect.top"),sQuery(id+"F0.wireOp",EDGE,"E52.rect.top"),sQuery(id+"F0.wireOp",EDGE,"E37.rect.bottom"),sQuery(id+"F0.wireOp",EDGE,"E47.rect.top"),sQuery(id+"F0.wireOp",EDGE,"E57.rect.bottom"),sQuery(id+"F0.wireOp",EDGE,"E35.rect.left"),sQuery(id+"F0.wireOp",EDGE,"E53.rect.bottom"),sQuery(id+"F0.wireOp",EDGE,"E52.rect.left"),sQuery(id+"F0.wireOp",EDGE,"E34.rect.left"),sQuery(id+"F0.wireOp",EDGE,"E34.rect.top"),sQuery(id+"F0.wireOp",EDGE,"E45.rect.bottom"),sQuery(id+"F0.wireOp",EDGE,"E52.rect.bottom"),sQuery(id+"F0.wireOp",EDGE,"E48.rect.top"),sQuery(id+"F0.wireOp",EDGE,"E43.rect.bottom"),sQuery(id+"F0.wireOp",EDGE,"E47.rect.right"),sQuery(id+"F0.wireOp",EDGE,"E58.rect.top"),sQuery(id+"F0.wireOp",EDGE,"E34.rect.right"),sQuery(id+"F0.wireOp",EDGE,"E50.rect.bottom"),sQuery(id+"F0.wireOp",EDGE,"E38.rect.bottom"),sQuery(id+"F0.wireOp",EDGE,"E44.rect.bottom"),sQuery(id+"F0.wireOp",EDGE,"E55.rect.bottom"),sQuery(id+"F0.wireOp",EDGE,"E36.rect.top"),sQuery(id+"F0.wireOp",EDGE,"E49.rect.top"),sQuery(id+"F0.wireOp",EDGE,"E39.rect.top"),sQuery(id+"F0.wireOp",EDGE,"E41.rect.top"),sQuery(id+"F0.wireOp",EDGE,"E62.rect.bottom"),sQuery(id+"F0.wireOp",EDGE,"E40.rect.top"),sQuery(id+"F0.wireOp",EDGE,"E51.rect.bottom"),sQuery(id+"F0.wireOp",EDGE,"E33.rect.right"),sQuery(id+"F0.wireOp",EDGE,"E47.rect.left"),sQuery(id+"F0.wireOp",EDGE,"E37.rect.top"),sQuery(id+"F0.wireOp",EDGE,"E37.rect.left"),sQuery(id+"F0.wireOp",EDGE,"E37.rect.right"),sQuery(id+"F0.wireOp",EDGE,"E46.rect.top"),sQuery(id+"F0.wireOp",EDGE,"E33.rect.bottom"),sQuery(id+"F0.wireOp",EDGE,"E44.rect.left"),sQuery(id+"F0.wireOp",EDGE,"E35.rect.top"),sQuery(id+"F0.wireOp",EDGE,"E44.rect.right"),sQuery(id+"F0.wireOp",EDGE,"E35.rect.bottom"),sQuery(id+"F0.wireOp",EDGE,"E42.rect.top"),sQuery(id+"F0.wireOp",EDGE,"E33.rect.left"),sQuery(id+"F0.wireOp",EDGE,"E35.rect.right"),sQuery(id+"F0.wireOp",EDGE,"E52.rect.right"),sQuery(id+"F0.wireOp",EDGE,"E62.rect.left"),sQuery(id+"F0.wireOp",EDGE,"E38.rect.top"),sQuery(id+"F0.wireOp",EDGE,"E41.rect.left"),sQuery(id+"F0.wireOp",EDGE,"E51.rect.top"),sQuery(id+"F0.wireOp",EDGE,"E59.rect.top"),sQuery(id+"F0.wireOp",EDGE,"E40.rect.bottom"),sQuery(id+"F0.wireOp",EDGE,"E43.rect.right"),sQuery(id+"F0.wireOp",EDGE,"E56.rect.bottom"),sQuery(id+"F0.wireOp",EDGE,"E53.rect.left"),sQuery(id+"F0.wireOp",EDGE,"E39.rect.left"),sQuery(id+"F0.wireOp",EDGE,"E47.rect.bottom"),sQuery(id+"F0.wireOp",EDGE,"E46.rect.right"),sQuery(id+"F0.wireOp",EDGE,"E41.rect.bottom"),sQuery(id+"F0.wireOp",EDGE,"E43.rect.left"),sQuery(id+"F0.wireOp",EDGE,"E57.rect.right"),sQuery(id+"F0.wireOp",EDGE,"E53.rect.top"),sQuery(id+"F0.wireOp",EDGE,"E56.rect.top"),sQuery(id+"F0.wireOp",EDGE,"E61.rect.bottom"),sQuery(id+"F0.wireOp",EDGE,"E40.rect.left"),sQuery(id+"F0.wireOp",EDGE,"E50.rect.top"),sQuery(id+"F0.wireOp",EDGE,"E46.rect.bottom"),sQuery(id+"F0.wireOp",EDGE,"E43.rect.top"),sQuery(id+"F0.wireOp",EDGE,"E57.rect.left"),sQuery(id+"F0.wireOp",EDGE,"E57.rect.top"),sQuery(id+"F0.wireOp",EDGE,"E61.rect.left"),sQuery(id+"F0.wireOp",EDGE,"E45.rect.top"),sQuery(id+"F0.wireOp",EDGE,"E51.rect.left"),sQuery(id+"F0.wireOp",EDGE,"E34.rect.bottom"),sQuery(id+"F0.wireOp",EDGE,"E48.rect.bottom"),sQuery(id+"F0.wireOp",EDGE,"E36.rect.right"),sQuery(id+"F0.wireOp",EDGE,"E56.rect.right"),sQuery(id+"F0.wireOp",EDGE,"E38.rect.right"),sQuery(id+"F0.wireOp",EDGE,"E48.rect.left"),sQuery(id+"F0.wireOp",EDGE,"E50.rect.right"),sQuery(id+"F0.wireOp",EDGE,"E45.rect.right"),sQuery(id+"F0.wireOp",EDGE,"E39.rect.bottom"),sQuery(id+"F0.wireOp",EDGE,"E55.rect.right"),sQuery(id+"F0.wireOp",EDGE,"E55.rect.left"),sQuery(id+"F0.wireOp",EDGE,"E55.rect.top"),sQuery(id+"F0.wireOp",EDGE,"E40.rect.right"),sQuery(id+"F0.wireOp",EDGE,"E62.rect.top"),sQuery(id+"F0.wireOp",EDGE,"E45.rect.left"),sQuery(id+"F0.wireOp",EDGE,"E50.rect.left"),sQuery(id+"F0.wireOp",EDGE,"E61.rect.right"),sQuery(id+"F0.wireOp",EDGE,"E39.rect.right"),sQuery(id+"F0.wireOp",EDGE,"E59.rect.right"),sQuery(id+"F0.wireOp",EDGE,"E53.rect.right"),sQuery(id+"F0.wireOp",EDGE,"E38.rect.left"),sQuery(id+"F0.wireOp",EDGE,"E36.rect.left"),sQuery(id+"F0.wireOp",EDGE,"E56.rect.left"),sQuery(id+"F0.wireOp",EDGE,"E61.rect.top"),sQuery(id+"F0.wireOp",EDGE,"E41.rect.right"),sQuery(id+"F0.wireOp",EDGE,"E59.rect.bottom"),sQuery(id+"F0.wireOp",EDGE,"E59.rect.left"),sQuery(id+"F0.wireOp",EDGE,"E46.rect.left"),sQuery(id+"F0.wireOp",EDGE,"E51.rect.right"),sQuery(id+"F0.wireOp",EDGE,"E48.rect.right"),sQuery(id+"F0.wireOp",EDGE,"E36.rect.bottom"),sQuery(id+"F0.wireOp",EDGE,"E60.rect.top"),sQuery(id+"F0.wireOp",EDGE,"E62.rect.right"),sQuery(id+"F0.wireOp",EDGE,"E42.rect.left"),sQuery(id+"F0.wireOp",EDGE,"E54.rect.bottom"),sQuery(id+"F0.wireOp",EDGE,"E60.rect.left"),sQuery(id+"F0.wireOp",EDGE,"E54.rect.top"),sQuery(id+"F0.wireOp",EDGE,"E60.rect.bottom"),sQuery(id+"F0.wireOp",EDGE,"E42.rect.right"),sQuery(id+"F0.wireOp",EDGE,"E60.rect.right"),sQuery(id+"F0.wireOp",EDGE,"E54.rect.right"),sQuery(id+"F0.wireOp",EDGE,"E49.rect.left"),sQuery(id+"F0.wireOp",EDGE,"E44.rect.top"),sQuery(id+"F0.wireOp",EDGE,"E58.rect.right"),sQuery(id+"F0.wireOp",EDGE,"E58.rect.bottom"),sQuery(id+"F0.wireOp",EDGE,"E33.rect.top"),sQuery(id+"F0.wireOp",EDGE,"E49.rect.bottom"),sQuery(id+"F0.wireOp",EDGE,"E49.rect.right"),sQuery(id+"F0.wireOp",EDGE,"E58.rect.left"),sQuery(id+"F0.wireOp",EDGE,"E54.rect.left"),sQuery(id+"F0.wireOp",EDGE,"E42.rect.bottom"),sQuery(id+"F0.wireOp",EDGE,"E63"),sQuery(id+"F0.wireOp",EDGE,"E64")])],"isStart":true});
            var sketch = newSketch(context, id + "F2", { "sketchPlane" : qUnion([Q0])});
            skLineSegment(sketch, "E65.bottom", {"start": v(-3, 3) * mm, "end": v(46.84, 3) * mm});
            skLineSegment(sketch, "E65.top", {"start": v(-3, -180.44) * mm, "end": v(46.84, -180.44) * mm});
            skLineSegment(sketch, "E65.left", {"start": v(-3, 3) * mm, "end": v(-3, -180.44) * mm});
            skLineSegment(sketch, "E65.right", {"start": v(46.84, 3) * mm, "end": v(46.84, -180.44) * mm});
            skCircle(sketch, "E66", {"center": v(43.84, 0) * mm, "radius": 1.38 * mm});
            skCircle(sketch, "E67", {"center": v(0, -177.44) * mm, "radius": 1.38 * mm});
            skSolve(sketch);
        }
        {
            var Q0;
            Q0 = qSketchRegion(id + "F2", true);
            extrude(context, id + "F3", {"entities" : qUnion([Q0]), "operationType" : NewBodyOperationType.ADD, "depth" : 4 * mm});
        }
        {
            var Q0;
            Q0=makeQuery(id+"F1.opExtrude","CAP_FACE",FACE,{"disambiguationData":[OSD([sQuery(id+"F0.wireOp",EDGE,"E0"),sQuery(id+"F0.wireOp",EDGE,"E1"),sQuery(id+"F0.wireOp",EDGE,"E2.bottom"),sQuery(id+"F0.wireOp",EDGE,"E2.top"),sQuery(id+"F0.wireOp",EDGE,"E2.left"),sQuery(id+"F0.wireOp",EDGE,"E2.right"),sQuery(id+"F0.wireOp",EDGE,"E3.rect.bottom"),sQuery(id+"F0.wireOp",EDGE,"E3.rect.top"),sQuery(id+"F0.wireOp",EDGE,"E3.rect.left"),sQuery(id+"F0.wireOp",EDGE,"E3.rect.right"),sQuery(id+"F0.wireOp",EDGE,"E4.rect.right"),sQuery(id+"F0.wireOp",EDGE,"E4.rect.left"),sQuery(id+"F0.wireOp",EDGE,"E4.rect.top"),sQuery(id+"F0.wireOp",EDGE,"E4.rect.bottom"),sQuery(id+"F0.wireOp",EDGE,"E5.rect.top"),sQuery(id+"F0.wireOp",EDGE,"E5.rect.bottom"),sQuery(id+"F0.wireOp",EDGE,"E5.rect.left"),sQuery(id+"F0.wireOp",EDGE,"E5.rect.right"),sQuery(id+"F0.wireOp",EDGE,"E6.rect.top"),sQuery(id+"F0.wireOp",EDGE,"E7.rect.left"),sQuery(id+"F0.wireOp",EDGE,"E6.rect.bottom"),sQuery(id+"F0.wireOp",EDGE,"E8.rect.top"),sQuery(id+"F0.wireOp",EDGE,"E7.rect.bottom"),sQuery(id+"F0.wireOp",EDGE,"E7.rect.top"),sQuery(id+"F0.wireOp",EDGE,"E8.rect.bottom"),sQuery(id+"F0.wireOp",EDGE,"E7.rect.right"),sQuery(id+"F0.wireOp",EDGE,"E8.rect.left"),sQuery(id+"F0.wireOp",EDGE,"E8.rect.right"),sQuery(id+"F0.wireOp",EDGE,"E6.rect.right"),sQuery(id+"F0.wireOp",EDGE,"E6.rect.left"),sQuery(id+"F0.wireOp",EDGE,"E11.rect.left"),sQuery(id+"F0.wireOp",EDGE,"E11.rect.bottom"),sQuery(id+"F0.wireOp",EDGE,"E10.rect.top"),sQuery(id+"F0.wireOp",EDGE,"E9.rect.right"),sQuery(id+"F0.wireOp",EDGE,"E10.rect.right"),sQuery(id+"F0.wireOp",EDGE,"E9.rect.top"),sQuery(id+"F0.wireOp",EDGE,"E11.rect.right"),sQuery(id+"F0.wireOp",EDGE,"E9.rect.bottom"),sQuery(id+"F0.wireOp",EDGE,"E9.rect.left"),sQuery(id+"F0.wireOp",EDGE,"E10.rect.left"),sQuery(id+"F0.wireOp",EDGE,"E11.rect.top"),sQuery(id+"F0.wireOp",EDGE,"E10.rect.bottom"),sQuery(id+"F0.wireOp",EDGE,"E14.rect.left"),sQuery(id+"F0.wireOp",EDGE,"E12.rect.right"),sQuery(id+"F0.wireOp",EDGE,"E17.rect.left"),sQuery(id+"F0.wireOp",EDGE,"E16.rect.left"),sQuery(id+"F0.wireOp",EDGE,"E13.rect.right"),sQuery(id+"F0.wireOp",EDGE,"E15.rect.right"),sQuery(id+"F0.wireOp",EDGE,"E17.rect.right"),sQuery(id+"F0.wireOp",EDGE,"E13.rect.left"),sQuery(id+"F0.wireOp",EDGE,"E16.rect.right"),sQuery(id+"F0.wireOp",EDGE,"E15.rect.left"),sQuery(id+"F0.wireOp",EDGE,"E14.rect.right"),sQuery(id+"F0.wireOp",EDGE,"E12.rect.left"),sQuery(id+"F0.wireOp",EDGE,"E15.rect.top"),sQuery(id+"F0.wireOp",EDGE,"E17.rect.bottom"),sQuery(id+"F0.wireOp",EDGE,"E13.rect.top"),sQuery(id+"F0.wireOp",EDGE,"E17.rect.top"),sQuery(id+"F0.wireOp",EDGE,"E12.rect.bottom"),sQuery(id+"F0.wireOp",EDGE,"E13.rect.bottom"),sQuery(id+"F0.wireOp",EDGE,"E12.rect.top"),sQuery(id+"F0.wireOp",EDGE,"E14.rect.top"),sQuery(id+"F0.wireOp",EDGE,"E14.rect.bottom"),sQuery(id+"F0.wireOp",EDGE,"E15.rect.bottom"),sQuery(id+"F0.wireOp",EDGE,"E16.rect.top"),sQuery(id+"F0.wireOp",EDGE,"E16.rect.bottom"),sQuery(id+"F0.wireOp",EDGE,"E19.rect.right"),sQuery(id+"F0.wireOp",EDGE,"E23.rect.left"),sQuery(id+"F0.wireOp",EDGE,"E25.rect.left"),sQuery(id+"F0.wireOp",EDGE,"E26.rect.right"),sQuery(id+"F0.wireOp",EDGE,"E27.rect.left"),sQuery(id+"F0.wireOp",EDGE,"E18.rect.right"),sQuery(id+"F0.wireOp",EDGE,"E21.rect.right"),sQuery(id+"F0.wireOp",EDGE,"E23.rect.right"),sQuery(id+"F0.wireOp",EDGE,"E19.rect.left"),sQuery(id+"F0.wireOp",EDGE,"E25.rect.right"),sQuery(id+"F0.wireOp",EDGE,"E26.rect.left"),sQuery(id+"F0.wireOp",EDGE,"E18.rect.left"),sQuery(id+"F0.wireOp",EDGE,"E28.rect.right"),sQuery(id+"F0.wireOp",EDGE,"E20.rect.right"),sQuery(id+"F0.wireOp",EDGE,"E27.rect.right"),sQuery(id+"F0.wireOp",EDGE,"E21.rect.left"),sQuery(id+"F0.wireOp",EDGE,"E28.rect.left"),sQuery(id+"F0.wireOp",EDGE,"E20.rect.left"),sQuery(id+"F0.wireOp",EDGE,"E24.rect.left"),sQuery(id+"F0.wireOp",EDGE,"E25.rect.bottom"),sQuery(id+"F0.wireOp",EDGE,"E21.rect.top"),sQuery(id+"F0.wireOp",EDGE,"E23.rect.bottom"),sQuery(id+"F0.wireOp",EDGE,"E22.rect.right"),sQuery(id+"F0.wireOp",EDGE,"E29.rect.top"),sQuery(id+"F0.wireOp",EDGE,"E22.rect.bottom"),sQuery(id+"F0.wireOp",EDGE,"E29.rect.left"),sQuery(id+"F0.wireOp",EDGE,"E29.rect.bottom"),sQuery(id+"F0.wireOp",EDGE,"E18.rect.bottom"),sQuery(id+"F0.wireOp",EDGE,"E21.rect.bottom"),sQuery(id+"F0.wireOp",EDGE,"E20.rect.top"),sQuery(id+"F0.wireOp",EDGE,"E28.rect.bottom"),sQuery(id+"F0.wireOp",EDGE,"E24.rect.right"),sQuery(id+"F0.wireOp",EDGE,"E26.rect.top"),sQuery(id+"F0.wireOp",EDGE,"E24.rect.bottom"),sQuery(id+"F0.wireOp",EDGE,"E20.rect.bottom"),sQuery(id+"F0.wireOp",EDGE,"E19.rect.top"),sQuery(id+"F0.wireOp",EDGE,"E22.rect.top"),sQuery(id+"F0.wireOp",EDGE,"E24.rect.top"),sQuery(id+"F0.wireOp",EDGE,"E18.rect.top"),sQuery(id+"F0.wireOp",EDGE,"E28.rect.top"),sQuery(id+"F0.wireOp",EDGE,"E26.rect.bottom"),sQuery(id+"F0.wireOp",EDGE,"E19.rect.bottom"),sQuery(id+"F0.wireOp",EDGE,"E23.rect.top"),sQuery(id+"F0.wireOp",EDGE,"E22.rect.left"),sQuery(id+"F0.wireOp",EDGE,"E27.rect.bottom"),sQuery(id+"F0.wireOp",EDGE,"E27.rect.top"),sQuery(id+"F0.wireOp",EDGE,"E25.rect.top"),sQuery(id+"F0.wireOp",EDGE,"E29.rect.right"),sQuery(id+"F0.wireOp",EDGE,"E32.rect.left"),sQuery(id+"F0.wireOp",EDGE,"E31.rect.right"),sQuery(id+"F0.wireOp",EDGE,"E30.rect.right"),sQuery(id+"F0.wireOp",EDGE,"E30.rect.left"),sQuery(id+"F0.wireOp",EDGE,"E32.rect.right"),sQuery(id+"F0.wireOp",EDGE,"E31.rect.left"),sQuery(id+"F0.wireOp",EDGE,"E30.rect.bottom"),sQuery(id+"F0.wireOp",EDGE,"E31.rect.top"),sQuery(id+"F0.wireOp",EDGE,"E31.rect.bottom"),sQuery(id+"F0.wireOp",EDGE,"E32.rect.bottom"),sQuery(id+"F0.wireOp",EDGE,"E32.rect.top"),sQuery(id+"F0.wireOp",EDGE,"E30.rect.top"),sQuery(id+"F0.wireOp",EDGE,"E52.rect.top"),sQuery(id+"F0.wireOp",EDGE,"E37.rect.bottom"),sQuery(id+"F0.wireOp",EDGE,"E47.rect.top"),sQuery(id+"F0.wireOp",EDGE,"E57.rect.bottom"),sQuery(id+"F0.wireOp",EDGE,"E35.rect.left"),sQuery(id+"F0.wireOp",EDGE,"E53.rect.bottom"),sQuery(id+"F0.wireOp",EDGE,"E52.rect.left"),sQuery(id+"F0.wireOp",EDGE,"E34.rect.left"),sQuery(id+"F0.wireOp",EDGE,"E34.rect.top"),sQuery(id+"F0.wireOp",EDGE,"E45.rect.bottom"),sQuery(id+"F0.wireOp",EDGE,"E52.rect.bottom"),sQuery(id+"F0.wireOp",EDGE,"E48.rect.top"),sQuery(id+"F0.wireOp",EDGE,"E43.rect.bottom"),sQuery(id+"F0.wireOp",EDGE,"E47.rect.right"),sQuery(id+"F0.wireOp",EDGE,"E58.rect.top"),sQuery(id+"F0.wireOp",EDGE,"E34.rect.right"),sQuery(id+"F0.wireOp",EDGE,"E50.rect.bottom"),sQuery(id+"F0.wireOp",EDGE,"E38.rect.bottom"),sQuery(id+"F0.wireOp",EDGE,"E44.rect.bottom"),sQuery(id+"F0.wireOp",EDGE,"E55.rect.bottom"),sQuery(id+"F0.wireOp",EDGE,"E36.rect.top"),sQuery(id+"F0.wireOp",EDGE,"E49.rect.top"),sQuery(id+"F0.wireOp",EDGE,"E39.rect.top"),sQuery(id+"F0.wireOp",EDGE,"E41.rect.top"),sQuery(id+"F0.wireOp",EDGE,"E62.rect.bottom"),sQuery(id+"F0.wireOp",EDGE,"E40.rect.top"),sQuery(id+"F0.wireOp",EDGE,"E51.rect.bottom"),sQuery(id+"F0.wireOp",EDGE,"E33.rect.right"),sQuery(id+"F0.wireOp",EDGE,"E47.rect.left"),sQuery(id+"F0.wireOp",EDGE,"E37.rect.top"),sQuery(id+"F0.wireOp",EDGE,"E37.rect.left"),sQuery(id+"F0.wireOp",EDGE,"E37.rect.right"),sQuery(id+"F0.wireOp",EDGE,"E46.rect.top"),sQuery(id+"F0.wireOp",EDGE,"E33.rect.bottom"),sQuery(id+"F0.wireOp",EDGE,"E44.rect.left"),sQuery(id+"F0.wireOp",EDGE,"E35.rect.top"),sQuery(id+"F0.wireOp",EDGE,"E44.rect.right"),sQuery(id+"F0.wireOp",EDGE,"E35.rect.bottom"),sQuery(id+"F0.wireOp",EDGE,"E42.rect.top"),sQuery(id+"F0.wireOp",EDGE,"E33.rect.left"),sQuery(id+"F0.wireOp",EDGE,"E35.rect.right"),sQuery(id+"F0.wireOp",EDGE,"E52.rect.right"),sQuery(id+"F0.wireOp",EDGE,"E62.rect.left"),sQuery(id+"F0.wireOp",EDGE,"E38.rect.top"),sQuery(id+"F0.wireOp",EDGE,"E41.rect.left"),sQuery(id+"F0.wireOp",EDGE,"E51.rect.top"),sQuery(id+"F0.wireOp",EDGE,"E59.rect.top"),sQuery(id+"F0.wireOp",EDGE,"E40.rect.bottom"),sQuery(id+"F0.wireOp",EDGE,"E43.rect.right"),sQuery(id+"F0.wireOp",EDGE,"E56.rect.bottom"),sQuery(id+"F0.wireOp",EDGE,"E53.rect.left"),sQuery(id+"F0.wireOp",EDGE,"E39.rect.left"),sQuery(id+"F0.wireOp",EDGE,"E47.rect.bottom"),sQuery(id+"F0.wireOp",EDGE,"E46.rect.right"),sQuery(id+"F0.wireOp",EDGE,"E41.rect.bottom"),sQuery(id+"F0.wireOp",EDGE,"E43.rect.left"),sQuery(id+"F0.wireOp",EDGE,"E57.rect.right"),sQuery(id+"F0.wireOp",EDGE,"E53.rect.top"),sQuery(id+"F0.wireOp",EDGE,"E56.rect.top"),sQuery(id+"F0.wireOp",EDGE,"E61.rect.bottom"),sQuery(id+"F0.wireOp",EDGE,"E40.rect.left"),sQuery(id+"F0.wireOp",EDGE,"E50.rect.top"),sQuery(id+"F0.wireOp",EDGE,"E46.rect.bottom"),sQuery(id+"F0.wireOp",EDGE,"E43.rect.top"),sQuery(id+"F0.wireOp",EDGE,"E57.rect.left"),sQuery(id+"F0.wireOp",EDGE,"E57.rect.top"),sQuery(id+"F0.wireOp",EDGE,"E61.rect.left"),sQuery(id+"F0.wireOp",EDGE,"E45.rect.top"),sQuery(id+"F0.wireOp",EDGE,"E51.rect.left"),sQuery(id+"F0.wireOp",EDGE,"E34.rect.bottom"),sQuery(id+"F0.wireOp",EDGE,"E48.rect.bottom"),sQuery(id+"F0.wireOp",EDGE,"E36.rect.right"),sQuery(id+"F0.wireOp",EDGE,"E56.rect.right"),sQuery(id+"F0.wireOp",EDGE,"E38.rect.right"),sQuery(id+"F0.wireOp",EDGE,"E48.rect.left"),sQuery(id+"F0.wireOp",EDGE,"E50.rect.right"),sQuery(id+"F0.wireOp",EDGE,"E45.rect.right"),sQuery(id+"F0.wireOp",EDGE,"E39.rect.bottom"),sQuery(id+"F0.wireOp",EDGE,"E55.rect.right"),sQuery(id+"F0.wireOp",EDGE,"E55.rect.left"),sQuery(id+"F0.wireOp",EDGE,"E55.rect.top"),sQuery(id+"F0.wireOp",EDGE,"E40.rect.right"),sQuery(id+"F0.wireOp",EDGE,"E62.rect.top"),sQuery(id+"F0.wireOp",EDGE,"E45.rect.left"),sQuery(id+"F0.wireOp",EDGE,"E50.rect.left"),sQuery(id+"F0.wireOp",EDGE,"E61.rect.right"),sQuery(id+"F0.wireOp",EDGE,"E39.rect.right"),sQuery(id+"F0.wireOp",EDGE,"E59.rect.right"),sQuery(id+"F0.wireOp",EDGE,"E53.rect.right"),sQuery(id+"F0.wireOp",EDGE,"E38.rect.left"),sQuery(id+"F0.wireOp",EDGE,"E36.rect.left"),sQuery(id+"F0.wireOp",EDGE,"E56.rect.left"),sQuery(id+"F0.wireOp",EDGE,"E61.rect.top"),sQuery(id+"F0.wireOp",EDGE,"E41.rect.right"),sQuery(id+"F0.wireOp",EDGE,"E59.rect.bottom"),sQuery(id+"F0.wireOp",EDGE,"E59.rect.left"),sQuery(id+"F0.wireOp",EDGE,"E46.rect.left"),sQuery(id+"F0.wireOp",EDGE,"E51.rect.right"),sQuery(id+"F0.wireOp",EDGE,"E48.rect.right"),sQuery(id+"F0.wireOp",EDGE,"E36.rect.bottom"),sQuery(id+"F0.wireOp",EDGE,"E60.rect.top"),sQuery(id+"F0.wireOp",EDGE,"E62.rect.right"),sQuery(id+"F0.wireOp",EDGE,"E42.rect.left"),sQuery(id+"F0.wireOp",EDGE,"E54.rect.bottom"),sQuery(id+"F0.wireOp",EDGE,"E60.rect.left"),sQuery(id+"F0.wireOp",EDGE,"E54.rect.top"),sQuery(id+"F0.wireOp",EDGE,"E60.rect.bottom"),sQuery(id+"F0.wireOp",EDGE,"E42.rect.right"),sQuery(id+"F0.wireOp",EDGE,"E60.rect.right"),sQuery(id+"F0.wireOp",EDGE,"E54.rect.right"),sQuery(id+"F0.wireOp",EDGE,"E49.rect.left"),sQuery(id+"F0.wireOp",EDGE,"E44.rect.top"),sQuery(id+"F0.wireOp",EDGE,"E58.rect.right"),sQuery(id+"F0.wireOp",EDGE,"E58.rect.bottom"),sQuery(id+"F0.wireOp",EDGE,"E33.rect.top"),sQuery(id+"F0.wireOp",EDGE,"E49.rect.bottom"),sQuery(id+"F0.wireOp",EDGE,"E49.rect.right"),sQuery(id+"F0.wireOp",EDGE,"E58.rect.left"),sQuery(id+"F0.wireOp",EDGE,"E54.rect.left"),sQuery(id+"F0.wireOp",EDGE,"E42.rect.bottom"),sQuery(id+"F0.wireOp",EDGE,"E63"),sQuery(id+"F0.wireOp",EDGE,"E64")])],"isStart":false});
            var sketch = newSketch(context, id + "F4", { "sketchPlane" : qUnion([Q0])});
            skLineSegment(sketch, "E68.bottom", {"start": v(2, 25.32) * mm, "end": v(10.03, 25.32) * mm});
            skLineSegment(sketch, "E68.top", {"start": v(2, 18.42) * mm, "end": v(14.38, 18.42) * mm});
            skLineSegment(sketch, "E68.left", {"start": v(2, 25.32) * mm, "end": v(2, 18.42) * mm});
            skLineSegment(sketch, "E69.top", {"start": v(14.38, 31.7) * mm, "end": v(10.03, 31.7) * mm});
            skLineSegment(sketch, "E69.right", {"start": v(10.03, 25.32) * mm, "end": v(10.03, 31.7) * mm});
            skLineSegment(sketch, "E70", {"start": v(14.38, 31.7) * mm, "end": v(14.38, 18.42) * mm});
            skLineSegment(sketch, "E71.right", {"start": v(10.03, 42.03) * mm, "end": v(10.03, 48.41) * mm});
            skLineSegment(sketch, "E72", {"start": v(14.38, 48.41) * mm, "end": v(14.38, 35.13) * mm});
            skLineSegment(sketch, "E71.top", {"start": v(14.38, 48.41) * mm, "end": v(10.03, 48.41) * mm});
            skLineSegment(sketch, "E73.bottom", {"start": v(2, 42.03) * mm, "end": v(10.03, 42.03) * mm});
            skLineSegment(sketch, "E73.top", {"start": v(2, 35.13) * mm, "end": v(14.38, 35.13) * mm});
            skLineSegment(sketch, "E73.left", {"start": v(2, 42.03) * mm, "end": v(2, 35.13) * mm});
            skLineSegment(sketch, "E74.top", {"start": v(14.38, 81.84) * mm, "end": v(10.03, 81.84) * mm});
            skLineSegment(sketch, "E75", {"start": v(14.38, 81.84) * mm, "end": v(14.38, 68.56) * mm});
            skLineSegment(sketch, "E76.bottom", {"start": v(2, 75.46) * mm, "end": v(10.03, 75.46) * mm});
            skLineSegment(sketch, "E77", {"start": v(14.38, 65.12) * mm, "end": v(14.38, 51.84) * mm});
            skLineSegment(sketch, "E78.right", {"start": v(10.03, 58.75) * mm, "end": v(10.03, 65.12) * mm});
            skLineSegment(sketch, "E78.top", {"start": v(14.38, 65.12) * mm, "end": v(10.03, 65.12) * mm});
            skLineSegment(sketch, "E79.left", {"start": v(2, 58.75) * mm, "end": v(2, 51.84) * mm});
            skLineSegment(sketch, "E79.top", {"start": v(2, 51.84) * mm, "end": v(14.38, 51.84) * mm});
            skLineSegment(sketch, "E79.bottom", {"start": v(2, 58.75) * mm, "end": v(10.03, 58.75) * mm});
            skLineSegment(sketch, "E74.right", {"start": v(10.03, 75.46) * mm, "end": v(10.03, 81.84) * mm});
            skLineSegment(sketch, "E76.left", {"start": v(2, 75.46) * mm, "end": v(2, 68.56) * mm});
            skLineSegment(sketch, "E76.top", {"start": v(2, 68.56) * mm, "end": v(14.38, 68.56) * mm});
            skLineSegment(sketch, "E80.bottom", {"start": v(2, 108.89) * mm, "end": v(10.03, 108.89) * mm});
            skLineSegment(sketch, "E81.right", {"start": v(10.03, 92.17) * mm, "end": v(10.03, 98.55) * mm});
            skLineSegment(sketch, "E82.top", {"start": v(14.38, 148.7) * mm, "end": v(10.03, 148.7) * mm});
            skLineSegment(sketch, "E83.top", {"start": v(14.38, 115.26) * mm, "end": v(10.03, 115.26) * mm});
            skLineSegment(sketch, "E84.top", {"start": v(2, 118.7) * mm, "end": v(14.38, 118.7) * mm});
            skLineSegment(sketch, "E85", {"start": v(14.38, 115.26) * mm, "end": v(14.38, 101.98) * mm});
            skLineSegment(sketch, "E83.right", {"start": v(10.03, 108.89) * mm, "end": v(10.03, 115.26) * mm});
            skLineSegment(sketch, "E86.bottom", {"start": v(2, 142.31) * mm, "end": v(10.03, 142.31) * mm});
            skLineSegment(sketch, "E80.top", {"start": v(2, 101.98) * mm, "end": v(14.38, 101.98) * mm});
            skLineSegment(sketch, "E87.left", {"start": v(2, 92.17) * mm, "end": v(2, 85.27) * mm});
            skLineSegment(sketch, "E82.right", {"start": v(10.03, 142.31) * mm, "end": v(10.03, 148.7) * mm});
            skLineSegment(sketch, "E88", {"start": v(14.38, 131.98) * mm, "end": v(14.38, 118.7) * mm});
            skLineSegment(sketch, "E80.left", {"start": v(2, 108.89) * mm, "end": v(2, 101.98) * mm});
            skLineSegment(sketch, "E87.bottom", {"start": v(2, 92.17) * mm, "end": v(10.03, 92.17) * mm});
            skLineSegment(sketch, "E89", {"start": v(14.38, 148.7) * mm, "end": v(14.38, 135.41) * mm});
            skLineSegment(sketch, "E90", {"start": v(14.38, 98.55) * mm, "end": v(14.38, 85.27) * mm});
            skLineSegment(sketch, "E87.top", {"start": v(2, 85.27) * mm, "end": v(14.38, 85.27) * mm});
            skLineSegment(sketch, "E84.left", {"start": v(2, 125.6) * mm, "end": v(2, 118.7) * mm});
            skLineSegment(sketch, "E84.bottom", {"start": v(2, 125.6) * mm, "end": v(10.03, 125.6) * mm});
            skLineSegment(sketch, "E86.top", {"start": v(2, 135.41) * mm, "end": v(14.38, 135.41) * mm});
            skLineSegment(sketch, "E91.right", {"start": v(10.03, 125.6) * mm, "end": v(10.03, 131.98) * mm});
            skLineSegment(sketch, "E86.left", {"start": v(2, 142.31) * mm, "end": v(2, 135.41) * mm});
            skLineSegment(sketch, "E81.top", {"start": v(14.38, 98.55) * mm, "end": v(10.03, 98.55) * mm});
            skLineSegment(sketch, "E91.top", {"start": v(14.38, 131.98) * mm, "end": v(10.03, 131.98) * mm});
            skLineSegment(sketch, "E92.top", {"start": v(2, 152.12) * mm, "end": v(14.38, 152.12) * mm});
            skLineSegment(sketch, "E92.left", {"start": v(2, 159.03) * mm, "end": v(2, 152.12) * mm});
            skLineSegment(sketch, "E93", {"start": v(14.38, 165.4) * mm, "end": v(14.38, 152.12) * mm});
            skLineSegment(sketch, "E94.top", {"start": v(14.38, 165.4) * mm, "end": v(10.03, 165.4) * mm});
            skLineSegment(sketch, "E94.right", {"start": v(10.03, 159.03) * mm, "end": v(10.03, 165.4) * mm});
            skLineSegment(sketch, "E92.bottom", {"start": v(2, 159.03) * mm, "end": v(10.03, 159.03) * mm});
            skLineSegment(sketch, "E95.left", {"start": v(22.7, 58.75) * mm, "end": v(22.7, 51.84) * mm});
            skLineSegment(sketch, "E96.top", {"start": v(22.7, 68.56) * mm, "end": v(31.15, 68.56) * mm});
            skLineSegment(sketch, "E97.top", {"start": v(22.7, 18.42) * mm, "end": v(31.15, 18.42) * mm});
            skLineSegment(sketch, "E97.bottom", {"start": v(22.7, 25.32) * mm, "end": v(26.8, 25.32) * mm});
            skLineSegment(sketch, "E98.left", {"start": v(22.7, 8.6) * mm, "end": v(22.7, 1.7) * mm});
            skLineSegment(sketch, "E98.top", {"start": v(22.7, 1.7) * mm, "end": v(31.15, 1.7) * mm});
            skLineSegment(sketch, "E95.top", {"start": v(22.7, 51.84) * mm, "end": v(31.15, 51.84) * mm});
            skLineSegment(sketch, "E98.bottom", {"start": v(22.7, 8.6) * mm, "end": v(26.8, 8.6) * mm});
            skLineSegment(sketch, "E95.bottom", {"start": v(22.7, 58.75) * mm, "end": v(26.8, 58.75) * mm});
            skLineSegment(sketch, "E99", {"start": v(31.15, 98.55) * mm, "end": v(31.15, 85.27) * mm});
            skLineSegment(sketch, "E100", {"start": v(31.15, 14.98) * mm, "end": v(31.15, 1.7) * mm});
            skLineSegment(sketch, "E101", {"start": v(31.15, 81.84) * mm, "end": v(31.15, 68.56) * mm});
            skLineSegment(sketch, "E102", {"start": v(31.15, 65.12) * mm, "end": v(31.15, 51.84) * mm});
            skLineSegment(sketch, "E103.top", {"start": v(22.7, 118.7) * mm, "end": v(31.15, 118.7) * mm});
            skLineSegment(sketch, "E97.left", {"start": v(22.7, 25.32) * mm, "end": v(22.7, 18.42) * mm});
            skLineSegment(sketch, "E104.left", {"start": v(22.7, 108.89) * mm, "end": v(22.7, 101.98) * mm});
            skLineSegment(sketch, "E104.top", {"start": v(22.7, 101.98) * mm, "end": v(31.15, 101.98) * mm});
            skLineSegment(sketch, "E104.bottom", {"start": v(22.7, 108.89) * mm, "end": v(26.8, 108.89) * mm});
            skLineSegment(sketch, "E105", {"start": v(31.15, 48.41) * mm, "end": v(31.15, 35.13) * mm});
            skLineSegment(sketch, "E103.left", {"start": v(22.7, 125.6) * mm, "end": v(22.7, 118.7) * mm});
            skLineSegment(sketch, "E106.bottom", {"start": v(22.7, 92.17) * mm, "end": v(26.8, 92.17) * mm});
            skLineSegment(sketch, "E107", {"start": v(31.15, 31.7) * mm, "end": v(31.15, 18.42) * mm});
            skLineSegment(sketch, "E108", {"start": v(31.15, 131.98) * mm, "end": v(31.15, 118.7) * mm});
            skLineSegment(sketch, "E109.bottom", {"start": v(22.7, 142.31) * mm, "end": v(26.8, 142.31) * mm});
            skLineSegment(sketch, "E96.bottom", {"start": v(22.7, 75.46) * mm, "end": v(26.8, 75.46) * mm});
            skLineSegment(sketch, "E106.left", {"start": v(22.7, 92.17) * mm, "end": v(22.7, 85.27) * mm});
            skLineSegment(sketch, "E110.bottom", {"start": v(22.7, 42.03) * mm, "end": v(26.8, 42.03) * mm});
            skLineSegment(sketch, "E111", {"start": v(31.15, 115.26) * mm, "end": v(31.15, 101.98) * mm});
            skLineSegment(sketch, "E110.top", {"start": v(22.7, 35.13) * mm, "end": v(31.15, 35.13) * mm});
            skLineSegment(sketch, "E112", {"start": v(31.15, 148.7) * mm, "end": v(31.15, 135.41) * mm});
            skLineSegment(sketch, "E110.left", {"start": v(22.7, 42.03) * mm, "end": v(22.7, 35.13) * mm});
            skLineSegment(sketch, "E96.left", {"start": v(22.7, 75.46) * mm, "end": v(22.7, 68.56) * mm});
            skLineSegment(sketch, "E109.left", {"start": v(22.7, 142.31) * mm, "end": v(22.7, 135.41) * mm});
            skLineSegment(sketch, "E109.top", {"start": v(22.7, 135.41) * mm, "end": v(31.15, 135.41) * mm});
            skLineSegment(sketch, "E106.top", {"start": v(22.7, 85.27) * mm, "end": v(31.15, 85.27) * mm});
            skLineSegment(sketch, "E103.bottom", {"start": v(22.7, 125.6) * mm, "end": v(26.8, 125.6) * mm});
            skLineSegment(sketch, "E113.right", {"start": v(26.8, 142.31) * mm, "end": v(26.8, 148.7) * mm});
            skLineSegment(sketch, "E113.top", {"start": v(31.15, 148.7) * mm, "end": v(26.8, 148.7) * mm});
            skLineSegment(sketch, "E114.right", {"start": v(26.8, 92.17) * mm, "end": v(26.8, 98.55) * mm});
            skLineSegment(sketch, "E115.right", {"start": v(26.8, 25.32) * mm, "end": v(26.8, 31.7) * mm});
            skLineSegment(sketch, "E115.top", {"start": v(31.15, 31.7) * mm, "end": v(26.8, 31.7) * mm});
            skLineSegment(sketch, "E116.top", {"start": v(31.15, 131.98) * mm, "end": v(26.8, 131.98) * mm});
            skLineSegment(sketch, "E117.top", {"start": v(31.15, 81.84) * mm, "end": v(26.8, 81.84) * mm});
            skLineSegment(sketch, "E118.right", {"start": v(26.8, 8.6) * mm, "end": v(26.8, 14.98) * mm});
            skLineSegment(sketch, "E114.top", {"start": v(31.15, 98.55) * mm, "end": v(26.8, 98.55) * mm});
            skLineSegment(sketch, "E119.top", {"start": v(31.15, 65.12) * mm, "end": v(26.8, 65.12) * mm});
            skLineSegment(sketch, "E120.right", {"start": v(26.8, 108.89) * mm, "end": v(26.8, 115.26) * mm});
            skLineSegment(sketch, "E118.top", {"start": v(31.15, 14.98) * mm, "end": v(26.8, 14.98) * mm});
            skLineSegment(sketch, "E117.right", {"start": v(26.8, 75.46) * mm, "end": v(26.8, 81.84) * mm});
            skLineSegment(sketch, "E119.right", {"start": v(26.8, 58.75) * mm, "end": v(26.8, 65.12) * mm});
            skLineSegment(sketch, "E116.right", {"start": v(26.8, 125.6) * mm, "end": v(26.8, 131.98) * mm});
            skLineSegment(sketch, "E121.top", {"start": v(31.15, 48.41) * mm, "end": v(26.8, 48.41) * mm});
            skLineSegment(sketch, "E121.right", {"start": v(26.8, 42.03) * mm, "end": v(26.8, 48.41) * mm});
            skLineSegment(sketch, "E120.top", {"start": v(31.15, 115.26) * mm, "end": v(26.8, 115.26) * mm});
            skLineSegment(sketch, "E122.bottom", {"start": v(22.7, 159.03) * mm, "end": v(26.8, 159.03) * mm});
            skLineSegment(sketch, "E123.top", {"start": v(31.15, 165.4) * mm, "end": v(26.8, 165.4) * mm});
            skLineSegment(sketch, "E123.right", {"start": v(26.8, 159.03) * mm, "end": v(26.8, 165.4) * mm});
            skLineSegment(sketch, "E122.top", {"start": v(22.7, 152.12) * mm, "end": v(31.15, 152.12) * mm});
            skLineSegment(sketch, "E122.left", {"start": v(22.7, 159.03) * mm, "end": v(22.7, 152.12) * mm});
            skLineSegment(sketch, "E124", {"start": v(31.15, 165.4) * mm, "end": v(31.15, 152.12) * mm});
            skLineSegment(sketch, "E125.bottom", {"start": v(3.5, 8.6) * mm, "end": v(10.03, 8.6) * mm});
            skLineSegment(sketch, "E125.top", {"start": v(3.5, 3.5) * mm, "end": v(14.38, 3.5) * mm});
            skLineSegment(sketch, "E125.left", {"start": v(3.5, 8.6) * mm, "end": v(3.5, 3.5) * mm});
            skLineSegment(sketch, "E126.right", {"start": v(10.03, 8.6) * mm, "end": v(10.03, 14.98) * mm});
            skLineSegment(sketch, "E126.top", {"start": v(14.38, 14.98) * mm, "end": v(10.03, 14.98) * mm});
            skLineSegment(sketch, "E127", {"start": v(14.38, 14.98) * mm, "end": v(14.38, 3.5) * mm});
            skLineSegment(sketch, "E128.bottom", {"start": v(22.8, 175.74) * mm, "end": v(26.9, 175.74) * mm});
            skLineSegment(sketch, "E128.left", {"start": v(22.8, 175.74) * mm, "end": v(22.8, 168.84) * mm});
            skLineSegment(sketch, "E129.top", {"start": v(3.37, 168.84) * mm, "end": v(14.5, 168.84) * mm});
            skLineSegment(sketch, "E128.top", {"start": v(22.8, 168.84) * mm, "end": v(31.25, 168.84) * mm});
            skLineSegment(sketch, "E130", {"start": v(31.25, 175.74) * mm, "end": v(31.25, 168.84) * mm});
            skLineSegment(sketch, "E131", {"start": v(14.5, 174.07) * mm, "end": v(14.5, 168.84) * mm});
            skLineSegment(sketch, "E132", {"start": v(26.9, 175.74) * mm, "end": v(31.25, 175.74) * mm});
            skLineSegment(sketch, "E133.bottom", {"start": v(43.84, 4.38) * mm, "end": v(39.46, 4.38) * mm});
            skLineSegment(sketch, "E133.top", {"start": v(43.84, 20.8) * mm, "end": v(39.46, 20.8) * mm});
            skLineSegment(sketch, "E133.left", {"start": v(43.84, 4.38) * mm, "end": v(43.84, 20.8) * mm});
            skLineSegment(sketch, "E133.right", {"start": v(39.46, 4.38) * mm, "end": v(39.46, 20.8) * mm});
            skLineSegment(sketch, "E134.right", {"start": v(39.46, 24) * mm, "end": v(39.46, 37.5) * mm});
            skLineSegment(sketch, "E134.left", {"start": v(43.84, 24) * mm, "end": v(43.84, 37.5) * mm});
            skLineSegment(sketch, "E134.bottom", {"start": v(43.84, 24) * mm, "end": v(39.46, 24) * mm});
            skLineSegment(sketch, "E134.top", {"start": v(43.84, 37.5) * mm, "end": v(39.46, 37.5) * mm});
            skLineSegment(sketch, "E135.left", {"start": v(43.84, 40.7) * mm, "end": v(43.84, 54.42) * mm});
            skLineSegment(sketch, "E135.bottom", {"start": v(43.84, 40.7) * mm, "end": v(39.46, 40.7) * mm});
            skLineSegment(sketch, "E135.right", {"start": v(39.46, 40.7) * mm, "end": v(39.46, 54.42) * mm});
            skLineSegment(sketch, "E136.right", {"start": v(39.46, 57.62) * mm, "end": v(39.46, 71.33) * mm});
            skLineSegment(sketch, "E136.left", {"start": v(43.84, 57.62) * mm, "end": v(43.84, 71.33) * mm});
            skLineSegment(sketch, "E136.bottom", {"start": v(43.84, 57.62) * mm, "end": v(39.46, 57.62) * mm});
            skLineSegment(sketch, "E136.top", {"start": v(43.84, 71.33) * mm, "end": v(39.46, 71.33) * mm});
            skLineSegment(sketch, "E135.top", {"start": v(43.84, 54.42) * mm, "end": v(39.46, 54.42) * mm});
            skLineSegment(sketch, "E137.right", {"start": v(39.46, 125.27) * mm, "end": v(39.46, 138.99) * mm});
            skLineSegment(sketch, "E138.left", {"start": v(43.84, 108.36) * mm, "end": v(43.84, 122.07) * mm});
            skLineSegment(sketch, "E139.left", {"start": v(43.84, 91.45) * mm, "end": v(43.84, 105.16) * mm});
            skLineSegment(sketch, "E139.right", {"start": v(39.46, 91.45) * mm, "end": v(39.46, 105.16) * mm});
            skLineSegment(sketch, "E140.right", {"start": v(39.46, 74.53) * mm, "end": v(39.46, 88.25) * mm});
            skLineSegment(sketch, "E140.left", {"start": v(43.84, 74.53) * mm, "end": v(43.84, 88.25) * mm});
            skLineSegment(sketch, "E138.right", {"start": v(39.46, 108.36) * mm, "end": v(39.46, 122.07) * mm});
            skLineSegment(sketch, "E140.bottom", {"start": v(43.84, 74.53) * mm, "end": v(39.46, 74.53) * mm});
            skLineSegment(sketch, "E137.top", {"start": v(43.84, 138.99) * mm, "end": v(39.46, 138.99) * mm});
            skLineSegment(sketch, "E137.left", {"start": v(43.84, 125.27) * mm, "end": v(43.84, 138.99) * mm});
            skLineSegment(sketch, "E137.bottom", {"start": v(43.84, 125.27) * mm, "end": v(39.46, 125.27) * mm});
            skLineSegment(sketch, "E138.bottom", {"start": v(43.84, 108.36) * mm, "end": v(39.46, 108.36) * mm});
            skLineSegment(sketch, "E139.top", {"start": v(43.84, 105.16) * mm, "end": v(39.46, 105.16) * mm});
            skLineSegment(sketch, "E139.bottom", {"start": v(43.84, 91.45) * mm, "end": v(39.46, 91.45) * mm});
            skLineSegment(sketch, "E140.top", {"start": v(43.84, 88.25) * mm, "end": v(39.46, 88.25) * mm});
            skLineSegment(sketch, "E138.top", {"start": v(43.84, 122.07) * mm, "end": v(39.46, 122.07) * mm});
            skLineSegment(sketch, "E141.bottom", {"start": v(43.45, 142.19) * mm, "end": v(39.07, 142.19) * mm});
            skLineSegment(sketch, "E142.left", {"start": v(43.45, 159.1) * mm, "end": v(43.45, 172.94) * mm});
            skLineSegment(sketch, "E142.top", {"start": v(43.45, 172.94) * mm, "end": v(39.07, 172.94) * mm});
            skLineSegment(sketch, "E141.right", {"start": v(39.07, 142.19) * mm, "end": v(39.07, 155.9) * mm});
            skLineSegment(sketch, "E142.right", {"start": v(39.07, 159.1) * mm, "end": v(39.07, 172.94) * mm});
            skLineSegment(sketch, "E141.left", {"start": v(43.45, 142.19) * mm, "end": v(43.45, 155.9) * mm});
            skLineSegment(sketch, "E142.bottom", {"start": v(43.45, 159.1) * mm, "end": v(39.07, 159.1) * mm});
            skLineSegment(sketch, "E141.top", {"start": v(43.45, 155.9) * mm, "end": v(39.07, 155.9) * mm});
            skLineSegment(sketch, "E143", {"start": v(3.37, 174.07) * mm, "end": v(14.5, 174.07) * mm});
            skLineSegment(sketch, "E144", {"start": v(3.37, 174.07) * mm, "end": v(3.37, 168.84) * mm});
            skSolve(sketch);
        }
        {
            var Q0;
            Q0 = qSketchRegion(id + "F4", true);
            extrude(context, id + "F5", {"entities" : qUnion([Q0]), "operationType" : NewBodyOperationType.REMOVE, "oppositeDirection" : true, "depth" : 25 * mm});
        }
        {
            var Q0;
            Q0=makeQuery(id+"F5.boolean.opBoolean","COPY",EDGE,{"derivedFrom":makeQuery(id+"F5.opExtrude","SWEPT_EDGE",EDGE,{"disambiguationData":[OSD([sQuery(id+"F4.wireOp",EDGE,"E129.top"),sQuery(id+"F4.wireOp",EDGE,"E144")])]})});
            var Q1;
            Q1=makeQuery(id+"F5.boolean.opBoolean","COPY",EDGE,{"derivedFrom":makeQuery(id+"F5.opExtrude","SWEPT_EDGE",EDGE,{"disambiguationData":[OSD([sQuery(id+"F4.wireOp",EDGE,"E131"),sQuery(id+"F4.wireOp",EDGE,"E143")])]})});
            var Q2;
            Q2=makeQuery(id+"F5.boolean.opBoolean","COPY",EDGE,{"derivedFrom":makeQuery(id+"F5.opExtrude","SWEPT_EDGE",EDGE,{"disambiguationData":[OSD([sQuery(id+"F4.wireOp",EDGE,"E143"),sQuery(id+"F4.wireOp",EDGE,"E144")])]})});
            var Q3;
            Q3=makeQuery(id+"F5.boolean.opBoolean","COPY",EDGE,{"derivedFrom":makeQuery(id+"F5.opExtrude","SWEPT_EDGE",EDGE,{"disambiguationData":[OSD([sQuery(id+"F4.wireOp",EDGE,"E129.top"),sQuery(id+"F4.wireOp",EDGE,"E131")])]})});
            var Q4;
            Q4=makeQuery(id+"F5.boolean.opBoolean","COPY",EDGE,{"derivedFrom":makeQuery(id+"F5.opExtrude","SWEPT_EDGE",EDGE,{"disambiguationData":[OSD([sQuery(id+"F4.wireOp",EDGE,"E128.bottom"),sQuery(id+"F4.wireOp",EDGE,"E128.left")])]})});
            var Q5;
            Q5=makeQuery(id+"F5.boolean.opBoolean","COPY",EDGE,{"derivedFrom":makeQuery(id+"F5.opExtrude","SWEPT_EDGE",EDGE,{"disambiguationData":[OSD([sQuery(id+"F4.wireOp",EDGE,"E130"),sQuery(id+"F4.wireOp",EDGE,"E132")])]})});
            var Q6;
            Q6=makeQuery(id+"F5.boolean.opBoolean","COPY",EDGE,{"derivedFrom":makeQuery(id+"F5.opExtrude","SWEPT_EDGE",EDGE,{"disambiguationData":[OSD([sQuery(id+"F4.wireOp",EDGE,"E128.left"),sQuery(id+"F4.wireOp",EDGE,"E128.top")])]})});
            var Q7;
            Q7=makeQuery(id+"F5.boolean.opBoolean","COPY",EDGE,{"derivedFrom":makeQuery(id+"F5.opExtrude","SWEPT_EDGE",EDGE,{"disambiguationData":[OSD([sQuery(id+"F4.wireOp",EDGE,"E92.top"),sQuery(id+"F4.wireOp",EDGE,"E92.left")])]})});
            var Q8;
            Q8=makeQuery(id+"F5.boolean.opBoolean","COPY",EDGE,{"derivedFrom":makeQuery(id+"F5.opExtrude","SWEPT_EDGE",EDGE,{"disambiguationData":[OSD([sQuery(id+"F4.wireOp",EDGE,"E122.top"),sQuery(id+"F4.wireOp",EDGE,"E122.left")])]})});
            var Q9;
            Q9=makeQuery(id+"F5.boolean.opBoolean","COPY",EDGE,{"derivedFrom":makeQuery(id+"F5.opExtrude","SWEPT_EDGE",EDGE,{"disambiguationData":[OSD([sQuery(id+"F4.wireOp",EDGE,"E86.top"),sQuery(id+"F4.wireOp",EDGE,"E86.left")])]})});
            var Q10;
            Q10=makeQuery(id+"F5.boolean.opBoolean","COPY",EDGE,{"derivedFrom":makeQuery(id+"F5.opExtrude","SWEPT_EDGE",EDGE,{"disambiguationData":[OSD([sQuery(id+"F4.wireOp",EDGE,"E109.left"),sQuery(id+"F4.wireOp",EDGE,"E109.top")])]})});
            var Q11;
            Q11=makeQuery(id+"F5.boolean.opBoolean","COPY",EDGE,{"derivedFrom":makeQuery(id+"F5.opExtrude","SWEPT_EDGE",EDGE,{"disambiguationData":[OSD([sQuery(id+"F4.wireOp",EDGE,"E94.top"),sQuery(id+"F4.wireOp",EDGE,"E94.right")])]})});
            var Q12;
            Q12=makeQuery(id+"F5.boolean.opBoolean","COPY",EDGE,{"derivedFrom":makeQuery(id+"F5.opExtrude","SWEPT_EDGE",EDGE,{"disambiguationData":[OSD([sQuery(id+"F4.wireOp",EDGE,"E93"),sQuery(id+"F4.wireOp",EDGE,"E94.top")])]})});
            var Q13;
            Q13=makeQuery(id+"F5.boolean.opBoolean","COPY",EDGE,{"derivedFrom":makeQuery(id+"F5.opExtrude","SWEPT_EDGE",EDGE,{"disambiguationData":[OSD([sQuery(id+"F4.wireOp",EDGE,"E123.top"),sQuery(id+"F4.wireOp",EDGE,"E124")])]})});
            var Q14;
            Q14=makeQuery(id+"F5.boolean.opBoolean","COPY",EDGE,{"derivedFrom":makeQuery(id+"F5.opExtrude","SWEPT_EDGE",EDGE,{"disambiguationData":[OSD([sQuery(id+"F4.wireOp",EDGE,"E142.left"),sQuery(id+"F4.wireOp",EDGE,"E142.top")])]})});
            var Q15;
            Q15=makeQuery(id+"F5.boolean.opBoolean","COPY",EDGE,{"derivedFrom":makeQuery(id+"F5.opExtrude","SWEPT_EDGE",EDGE,{"disambiguationData":[OSD([sQuery(id+"F4.wireOp",EDGE,"E112"),sQuery(id+"F4.wireOp",EDGE,"E113.top")])]})});
            var Q16;
            Q16=makeQuery(id+"F5.boolean.opBoolean","COPY",EDGE,{"derivedFrom":makeQuery(id+"F5.opExtrude","SWEPT_EDGE",EDGE,{"disambiguationData":[OSD([sQuery(id+"F4.wireOp",EDGE,"E122.bottom"),sQuery(id+"F4.wireOp",EDGE,"E122.left")])]})});
            var Q17;
            Q17=makeQuery(id+"F5.boolean.opBoolean","COPY",EDGE,{"derivedFrom":makeQuery(id+"F5.opExtrude","SWEPT_EDGE",EDGE,{"disambiguationData":[OSD([sQuery(id+"F4.wireOp",EDGE,"E123.top"),sQuery(id+"F4.wireOp",EDGE,"E123.right")])]})});
            var Q18;
            Q18=makeQuery(id+"F5.boolean.opBoolean","COPY",EDGE,{"derivedFrom":makeQuery(id+"F5.opExtrude","SWEPT_EDGE",EDGE,{"disambiguationData":[OSD([sQuery(id+"F4.wireOp",EDGE,"E142.top"),sQuery(id+"F4.wireOp",EDGE,"E142.right")])]})});
            var Q19;
            Q19=makeQuery(id+"F5.boolean.opBoolean","COPY",EDGE,{"derivedFrom":makeQuery(id+"F5.opExtrude","SWEPT_EDGE",EDGE,{"disambiguationData":[OSD([sQuery(id+"F4.wireOp",EDGE,"E142.right"),sQuery(id+"F4.wireOp",EDGE,"E142.bottom")])]})});
            var Q20;
            Q20=makeQuery(id+"F5.boolean.opBoolean","COPY",EDGE,{"derivedFrom":makeQuery(id+"F5.opExtrude","SWEPT_EDGE",EDGE,{"disambiguationData":[OSD([sQuery(id+"F4.wireOp",EDGE,"E142.left"),sQuery(id+"F4.wireOp",EDGE,"E142.bottom")])]})});
            var Q21;
            Q21=makeQuery(id+"F5.boolean.opBoolean","COPY",EDGE,{"derivedFrom":makeQuery(id+"F5.opExtrude","SWEPT_EDGE",EDGE,{"disambiguationData":[OSD([sQuery(id+"F4.wireOp",EDGE,"E141.right"),sQuery(id+"F4.wireOp",EDGE,"E141.top")])]})});
            var Q22;
            Q22=makeQuery(id+"F5.boolean.opBoolean","COPY",EDGE,{"derivedFrom":makeQuery(id+"F5.opExtrude","SWEPT_EDGE",EDGE,{"disambiguationData":[OSD([sQuery(id+"F4.wireOp",EDGE,"E141.left"),sQuery(id+"F4.wireOp",EDGE,"E141.top")])]})});
            var Q23;
            Q23=makeQuery(id+"F5.boolean.opBoolean","COPY",EDGE,{"derivedFrom":makeQuery(id+"F5.opExtrude","SWEPT_EDGE",EDGE,{"disambiguationData":[OSD([sQuery(id+"F4.wireOp",EDGE,"E141.bottom"),sQuery(id+"F4.wireOp",EDGE,"E141.right")])]})});
            var Q24;
            Q24=makeQuery(id+"F5.boolean.opBoolean","COPY",EDGE,{"derivedFrom":makeQuery(id+"F5.opExtrude","SWEPT_EDGE",EDGE,{"disambiguationData":[OSD([sQuery(id+"F4.wireOp",EDGE,"E141.bottom"),sQuery(id+"F4.wireOp",EDGE,"E141.left")])]})});
            var Q25;
            Q25=makeQuery(id+"F5.boolean.opBoolean","COPY",EDGE,{"derivedFrom":makeQuery(id+"F5.opExtrude","SWEPT_EDGE",EDGE,{"disambiguationData":[OSD([sQuery(id+"F4.wireOp",EDGE,"E113.right"),sQuery(id+"F4.wireOp",EDGE,"E113.top")])]})});
            var Q26;
            Q26=makeQuery(id+"F5.boolean.opBoolean","COPY",EDGE,{"derivedFrom":makeQuery(id+"F5.opExtrude","SWEPT_EDGE",EDGE,{"disambiguationData":[OSD([sQuery(id+"F4.wireOp",EDGE,"E82.top"),sQuery(id+"F4.wireOp",EDGE,"E82.right")])]})});
            var Q27;
            Q27=makeQuery(id+"F5.boolean.opBoolean","COPY",EDGE,{"derivedFrom":makeQuery(id+"F5.opExtrude","SWEPT_EDGE",EDGE,{"disambiguationData":[OSD([sQuery(id+"F4.wireOp",EDGE,"E86.bottom"),sQuery(id+"F4.wireOp",EDGE,"E86.left")])]})});
            var Q28;
            Q28=makeQuery(id+"F5.boolean.opBoolean","COPY",EDGE,{"derivedFrom":makeQuery(id+"F5.opExtrude","SWEPT_EDGE",EDGE,{"disambiguationData":[OSD([sQuery(id+"F4.wireOp",EDGE,"E92.left"),sQuery(id+"F4.wireOp",EDGE,"E92.bottom")])]})});
            var Q29;
            Q29=makeQuery(id+"F5.boolean.opBoolean","COPY",EDGE,{"derivedFrom":makeQuery(id+"F5.opExtrude","SWEPT_EDGE",EDGE,{"disambiguationData":[OSD([sQuery(id+"F4.wireOp",EDGE,"E109.bottom"),sQuery(id+"F4.wireOp",EDGE,"E109.left")])]})});
            var Q30;
            Q30=makeQuery(id+"F5.boolean.opBoolean","COPY",EDGE,{"derivedFrom":makeQuery(id+"F5.opExtrude","SWEPT_EDGE",EDGE,{"disambiguationData":[OSD([sQuery(id+"F4.wireOp",EDGE,"E137.right"),sQuery(id+"F4.wireOp",EDGE,"E137.top")])]})});
            var Q31;
            Q31=makeQuery(id+"F5.boolean.opBoolean","COPY",EDGE,{"derivedFrom":makeQuery(id+"F5.opExtrude","SWEPT_EDGE",EDGE,{"disambiguationData":[OSD([sQuery(id+"F4.wireOp",EDGE,"E116.top"),sQuery(id+"F4.wireOp",EDGE,"E116.right")])]})});
            var Q32;
            Q32=makeQuery(id+"F5.boolean.opBoolean","COPY",EDGE,{"derivedFrom":makeQuery(id+"F5.opExtrude","SWEPT_EDGE",EDGE,{"disambiguationData":[OSD([sQuery(id+"F4.wireOp",EDGE,"E103.left"),sQuery(id+"F4.wireOp",EDGE,"E103.bottom")])]})});
            var Q33;
            Q33=makeQuery(id+"F5.boolean.opBoolean","COPY",EDGE,{"derivedFrom":makeQuery(id+"F5.opExtrude","SWEPT_EDGE",EDGE,{"disambiguationData":[OSD([sQuery(id+"F4.wireOp",EDGE,"E91.right"),sQuery(id+"F4.wireOp",EDGE,"E91.top")])]})});
            var Q34;
            Q34=makeQuery(id+"F5.boolean.opBoolean","COPY",EDGE,{"derivedFrom":makeQuery(id+"F5.opExtrude","SWEPT_EDGE",EDGE,{"disambiguationData":[OSD([sQuery(id+"F4.wireOp",EDGE,"E84.left"),sQuery(id+"F4.wireOp",EDGE,"E84.bottom")])]})});
            var Q35;
            Q35=makeQuery(id+"F5.boolean.opBoolean","COPY",EDGE,{"derivedFrom":makeQuery(id+"F5.opExtrude","SWEPT_EDGE",EDGE,{"disambiguationData":[OSD([sQuery(id+"F4.wireOp",EDGE,"E80.bottom"),sQuery(id+"F4.wireOp",EDGE,"E80.left")])]})});
            var Q36;
            Q36=makeQuery(id+"F5.boolean.opBoolean","COPY",EDGE,{"derivedFrom":makeQuery(id+"F5.opExtrude","SWEPT_EDGE",EDGE,{"disambiguationData":[OSD([sQuery(id+"F4.wireOp",EDGE,"E83.top"),sQuery(id+"F4.wireOp",EDGE,"E83.right")])]})});
            var Q37;
            Q37=makeQuery(id+"F5.boolean.opBoolean","COPY",EDGE,{"derivedFrom":makeQuery(id+"F5.opExtrude","SWEPT_EDGE",EDGE,{"disambiguationData":[OSD([sQuery(id+"F4.wireOp",EDGE,"E104.left"),sQuery(id+"F4.wireOp",EDGE,"E104.bottom")])]})});
            var Q38;
            Q38=makeQuery(id+"F5.boolean.opBoolean","COPY",EDGE,{"derivedFrom":makeQuery(id+"F5.opExtrude","SWEPT_EDGE",EDGE,{"disambiguationData":[OSD([sQuery(id+"F4.wireOp",EDGE,"E120.right"),sQuery(id+"F4.wireOp",EDGE,"E120.top")])]})});
            var Q39;
            Q39=makeQuery(id+"F5.boolean.opBoolean","COPY",EDGE,{"derivedFrom":makeQuery(id+"F5.opExtrude","SWEPT_EDGE",EDGE,{"disambiguationData":[OSD([sQuery(id+"F4.wireOp",EDGE,"E138.right"),sQuery(id+"F4.wireOp",EDGE,"E138.top")])]})});
            var Q40;
            Q40=makeQuery(id+"F5.boolean.opBoolean","COPY",EDGE,{"derivedFrom":makeQuery(id+"F5.opExtrude","SWEPT_EDGE",EDGE,{"disambiguationData":[OSD([sQuery(id+"F4.wireOp",EDGE,"E139.right"),sQuery(id+"F4.wireOp",EDGE,"E139.top")])]})});
            var Q41;
            Q41=makeQuery(id+"F5.boolean.opBoolean","COPY",EDGE,{"derivedFrom":makeQuery(id+"F5.opExtrude","SWEPT_EDGE",EDGE,{"disambiguationData":[OSD([sQuery(id+"F4.wireOp",EDGE,"E114.right"),sQuery(id+"F4.wireOp",EDGE,"E114.top")])]})});
            var Q42;
            Q42=makeQuery(id+"F5.boolean.opBoolean","COPY",EDGE,{"derivedFrom":makeQuery(id+"F5.opExtrude","SWEPT_EDGE",EDGE,{"disambiguationData":[OSD([sQuery(id+"F4.wireOp",EDGE,"E106.bottom"),sQuery(id+"F4.wireOp",EDGE,"E106.left")])]})});
            var Q43;
            Q43=makeQuery(id+"F5.boolean.opBoolean","COPY",EDGE,{"derivedFrom":makeQuery(id+"F5.opExtrude","SWEPT_EDGE",EDGE,{"disambiguationData":[OSD([sQuery(id+"F4.wireOp",EDGE,"E140.right"),sQuery(id+"F4.wireOp",EDGE,"E140.top")])]})});
            var Q44;
            Q44=makeQuery(id+"F5.boolean.opBoolean","COPY",EDGE,{"derivedFrom":makeQuery(id+"F5.opExtrude","SWEPT_EDGE",EDGE,{"disambiguationData":[OSD([sQuery(id+"F4.wireOp",EDGE,"E117.top"),sQuery(id+"F4.wireOp",EDGE,"E117.right")])]})});
            var Q45;
            Q45=makeQuery(id+"F5.boolean.opBoolean","COPY",EDGE,{"derivedFrom":makeQuery(id+"F5.opExtrude","SWEPT_EDGE",EDGE,{"disambiguationData":[OSD([sQuery(id+"F4.wireOp",EDGE,"E96.bottom"),sQuery(id+"F4.wireOp",EDGE,"E96.left")])]})});
            var Q46;
            Q46=makeQuery(id+"F5.boolean.opBoolean","COPY",EDGE,{"derivedFrom":makeQuery(id+"F5.opExtrude","SWEPT_EDGE",EDGE,{"disambiguationData":[OSD([sQuery(id+"F4.wireOp",EDGE,"E81.right"),sQuery(id+"F4.wireOp",EDGE,"E81.top")])]})});
            var Q47;
            Q47=makeQuery(id+"F5.boolean.opBoolean","COPY",EDGE,{"derivedFrom":makeQuery(id+"F5.opExtrude","SWEPT_EDGE",EDGE,{"disambiguationData":[OSD([sQuery(id+"F4.wireOp",EDGE,"E87.left"),sQuery(id+"F4.wireOp",EDGE,"E87.bottom")])]})});
            var Q48;
            Q48=makeQuery(id+"F5.boolean.opBoolean","COPY",EDGE,{"derivedFrom":makeQuery(id+"F5.opExtrude","SWEPT_EDGE",EDGE,{"disambiguationData":[OSD([sQuery(id+"F4.wireOp",EDGE,"E74.top"),sQuery(id+"F4.wireOp",EDGE,"E74.right")])]})});
            var Q49;
            Q49=makeQuery(id+"F5.boolean.opBoolean","COPY",EDGE,{"derivedFrom":makeQuery(id+"F5.opExtrude","SWEPT_EDGE",EDGE,{"disambiguationData":[OSD([sQuery(id+"F4.wireOp",EDGE,"E76.bottom"),sQuery(id+"F4.wireOp",EDGE,"E76.left")])]})});
            var Q50;
            Q50=makeQuery(id+"F5.boolean.opBoolean","COPY",EDGE,{"derivedFrom":makeQuery(id+"F5.opExtrude","SWEPT_EDGE",EDGE,{"disambiguationData":[OSD([sQuery(id+"F4.wireOp",EDGE,"E78.right"),sQuery(id+"F4.wireOp",EDGE,"E78.top")])]})});
            var Q51;
            Q51=makeQuery(id+"F5.boolean.opBoolean","COPY",EDGE,{"derivedFrom":makeQuery(id+"F5.opExtrude","SWEPT_EDGE",EDGE,{"disambiguationData":[OSD([sQuery(id+"F4.wireOp",EDGE,"E79.left"),sQuery(id+"F4.wireOp",EDGE,"E79.bottom")])]})});
            var Q52;
            Q52=makeQuery(id+"F5.boolean.opBoolean","COPY",EDGE,{"derivedFrom":makeQuery(id+"F5.opExtrude","SWEPT_EDGE",EDGE,{"disambiguationData":[OSD([sQuery(id+"F4.wireOp",EDGE,"E95.left"),sQuery(id+"F4.wireOp",EDGE,"E95.bottom")])]})});
            var Q53;
            Q53=makeQuery(id+"F5.boolean.opBoolean","COPY",EDGE,{"derivedFrom":makeQuery(id+"F5.opExtrude","SWEPT_EDGE",EDGE,{"disambiguationData":[OSD([sQuery(id+"F4.wireOp",EDGE,"E119.top"),sQuery(id+"F4.wireOp",EDGE,"E119.right")])]})});
            var Q54;
            Q54=makeQuery(id+"F5.boolean.opBoolean","COPY",EDGE,{"derivedFrom":makeQuery(id+"F5.opExtrude","SWEPT_EDGE",EDGE,{"disambiguationData":[OSD([sQuery(id+"F4.wireOp",EDGE,"E121.top"),sQuery(id+"F4.wireOp",EDGE,"E121.right")])]})});
            var Q55;
            Q55=makeQuery(id+"F5.boolean.opBoolean","COPY",EDGE,{"derivedFrom":makeQuery(id+"F5.opExtrude","SWEPT_EDGE",EDGE,{"disambiguationData":[OSD([sQuery(id+"F4.wireOp",EDGE,"E110.bottom"),sQuery(id+"F4.wireOp",EDGE,"E110.left")])]})});
            var Q56;
            Q56=makeQuery(id+"F5.boolean.opBoolean","COPY",EDGE,{"derivedFrom":makeQuery(id+"F5.opExtrude","SWEPT_EDGE",EDGE,{"disambiguationData":[OSD([sQuery(id+"F4.wireOp",EDGE,"E71.right"),sQuery(id+"F4.wireOp",EDGE,"E71.top")])]})});
            var Q57;
            Q57=makeQuery(id+"F5.boolean.opBoolean","COPY",EDGE,{"derivedFrom":makeQuery(id+"F5.opExtrude","SWEPT_EDGE",EDGE,{"disambiguationData":[OSD([sQuery(id+"F4.wireOp",EDGE,"E73.bottom"),sQuery(id+"F4.wireOp",EDGE,"E73.left")])]})});
            var Q58;
            Q58=makeQuery(id+"F5.boolean.opBoolean","COPY",EDGE,{"derivedFrom":makeQuery(id+"F5.opExtrude","SWEPT_EDGE",EDGE,{"disambiguationData":[OSD([sQuery(id+"F4.wireOp",EDGE,"E115.right"),sQuery(id+"F4.wireOp",EDGE,"E115.top")])]})});
            var Q59;
            Q59=makeQuery(id+"F5.boolean.opBoolean","COPY",EDGE,{"derivedFrom":makeQuery(id+"F5.opExtrude","SWEPT_EDGE",EDGE,{"disambiguationData":[OSD([sQuery(id+"F4.wireOp",EDGE,"E97.bottom"),sQuery(id+"F4.wireOp",EDGE,"E97.left")])]})});
            var Q60;
            Q60=makeQuery(id+"F5.boolean.opBoolean","COPY",EDGE,{"derivedFrom":makeQuery(id+"F5.opExtrude","SWEPT_EDGE",EDGE,{"disambiguationData":[OSD([sQuery(id+"F4.wireOp",EDGE,"E136.right"),sQuery(id+"F4.wireOp",EDGE,"E136.top")])]})});
            var Q61;
            Q61=makeQuery(id+"F5.boolean.opBoolean","COPY",EDGE,{"derivedFrom":makeQuery(id+"F5.opExtrude","SWEPT_EDGE",EDGE,{"disambiguationData":[OSD([sQuery(id+"F4.wireOp",EDGE,"E135.right"),sQuery(id+"F4.wireOp",EDGE,"E135.top")])]})});
            var Q62;
            Q62=makeQuery(id+"F5.boolean.opBoolean","COPY",EDGE,{"derivedFrom":makeQuery(id+"F5.opExtrude","SWEPT_EDGE",EDGE,{"disambiguationData":[OSD([sQuery(id+"F4.wireOp",EDGE,"E134.right"),sQuery(id+"F4.wireOp",EDGE,"E134.top")])]})});
            var Q63;
            Q63=makeQuery(id+"F5.boolean.opBoolean","COPY",EDGE,{"derivedFrom":makeQuery(id+"F5.opExtrude","SWEPT_EDGE",EDGE,{"disambiguationData":[OSD([sQuery(id+"F4.wireOp",EDGE,"E133.top"),sQuery(id+"F4.wireOp",EDGE,"E133.right")])]})});
            var Q64;
            Q64=makeQuery(id+"F5.boolean.opBoolean","COPY",EDGE,{"derivedFrom":makeQuery(id+"F5.opExtrude","SWEPT_EDGE",EDGE,{"disambiguationData":[OSD([sQuery(id+"F4.wireOp",EDGE,"E118.right"),sQuery(id+"F4.wireOp",EDGE,"E118.top")])]})});
            var Q65;
            Q65=makeQuery(id+"F5.boolean.opBoolean","COPY",EDGE,{"derivedFrom":makeQuery(id+"F5.opExtrude","SWEPT_EDGE",EDGE,{"disambiguationData":[OSD([sQuery(id+"F4.wireOp",EDGE,"E98.left"),sQuery(id+"F4.wireOp",EDGE,"E98.bottom")])]})});
            var Q66;
            Q66=makeQuery(id+"F5.boolean.opBoolean","COPY",EDGE,{"derivedFrom":makeQuery(id+"F5.opExtrude","SWEPT_EDGE",EDGE,{"disambiguationData":[OSD([sQuery(id+"F4.wireOp",EDGE,"E69.top"),sQuery(id+"F4.wireOp",EDGE,"E69.right")])]})});
            var Q67;
            Q67=makeQuery(id+"F5.boolean.opBoolean","COPY",EDGE,{"derivedFrom":makeQuery(id+"F5.opExtrude","SWEPT_EDGE",EDGE,{"disambiguationData":[OSD([sQuery(id+"F4.wireOp",EDGE,"E68.bottom"),sQuery(id+"F4.wireOp",EDGE,"E68.left")])]})});
            var Q68;
            Q68=makeQuery(id+"F5.boolean.opBoolean","COPY",EDGE,{"derivedFrom":makeQuery(id+"F5.opExtrude","SWEPT_EDGE",EDGE,{"disambiguationData":[OSD([sQuery(id+"F4.wireOp",EDGE,"E126.right"),sQuery(id+"F4.wireOp",EDGE,"E126.top")])]})});
            var Q69;
            Q69=makeQuery(id+"F5.boolean.opBoolean","COPY",EDGE,{"derivedFrom":makeQuery(id+"F5.opExtrude","SWEPT_EDGE",EDGE,{"disambiguationData":[OSD([sQuery(id+"F4.wireOp",EDGE,"E125.bottom"),sQuery(id+"F4.wireOp",EDGE,"E125.left")])]})});
            var Q70;
            Q70=makeQuery(id+"F5.boolean.opBoolean","COPY",EDGE,{"derivedFrom":makeQuery(id+"F5.opExtrude","SWEPT_EDGE",EDGE,{"disambiguationData":[OSD([sQuery(id+"F4.wireOp",EDGE,"E128.top"),sQuery(id+"F4.wireOp",EDGE,"E130")])]})});
            var Q71;
            Q71=makeQuery(id+"F5.boolean.opBoolean","COPY",EDGE,{"derivedFrom":makeQuery(id+"F5.opExtrude","SWEPT_EDGE",EDGE,{"disambiguationData":[OSD([sQuery(id+"F4.wireOp",EDGE,"E122.top"),sQuery(id+"F4.wireOp",EDGE,"E124")])]})});
            var Q72;
            Q72=makeQuery(id+"F5.boolean.opBoolean","COPY",EDGE,{"derivedFrom":makeQuery(id+"F5.opExtrude","SWEPT_EDGE",EDGE,{"disambiguationData":[OSD([sQuery(id+"F4.wireOp",EDGE,"E137.left"),sQuery(id+"F4.wireOp",EDGE,"E137.bottom")])]})});
            var Q73;
            Q73=makeQuery(id+"F5.boolean.opBoolean","COPY",EDGE,{"derivedFrom":makeQuery(id+"F5.opExtrude","SWEPT_EDGE",EDGE,{"disambiguationData":[OSD([sQuery(id+"F4.wireOp",EDGE,"E112"),sQuery(id+"F4.wireOp",EDGE,"E109.top")])]})});
            var Q74;
            Q74=makeQuery(id+"F5.boolean.opBoolean","COPY",EDGE,{"derivedFrom":makeQuery(id+"F5.opExtrude","SWEPT_EDGE",EDGE,{"disambiguationData":[OSD([sQuery(id+"F4.wireOp",EDGE,"E138.left"),sQuery(id+"F4.wireOp",EDGE,"E138.bottom")])]})});
            var Q75;
            Q75=makeQuery(id+"F5.boolean.opBoolean","COPY",EDGE,{"derivedFrom":makeQuery(id+"F5.opExtrude","SWEPT_EDGE",EDGE,{"disambiguationData":[OSD([sQuery(id+"F4.wireOp",EDGE,"E103.top"),sQuery(id+"F4.wireOp",EDGE,"E108")])]})});
            var Q76;
            Q76=makeQuery(id+"F5.boolean.opBoolean","COPY",EDGE,{"derivedFrom":makeQuery(id+"F5.opExtrude","SWEPT_EDGE",EDGE,{"disambiguationData":[OSD([sQuery(id+"F4.wireOp",EDGE,"E89"),sQuery(id+"F4.wireOp",EDGE,"E86.top")])]})});
            var Q77;
            Q77=makeQuery(id+"F5.boolean.opBoolean","COPY",EDGE,{"derivedFrom":makeQuery(id+"F5.opExtrude","SWEPT_EDGE",EDGE,{"disambiguationData":[OSD([sQuery(id+"F4.wireOp",EDGE,"E92.top"),sQuery(id+"F4.wireOp",EDGE,"E93")])]})});
            var Q78;
            Q78=makeQuery(id+"F5.boolean.opBoolean","COPY",EDGE,{"derivedFrom":makeQuery(id+"F5.opExtrude","SWEPT_EDGE",EDGE,{"disambiguationData":[OSD([sQuery(id+"F4.wireOp",EDGE,"E84.top"),sQuery(id+"F4.wireOp",EDGE,"E88")])]})});
            var Q79;
            Q79=makeQuery(id+"F5.boolean.opBoolean","COPY",EDGE,{"derivedFrom":makeQuery(id+"F5.opExtrude","SWEPT_EDGE",EDGE,{"disambiguationData":[OSD([sQuery(id+"F4.wireOp",EDGE,"E104.top"),sQuery(id+"F4.wireOp",EDGE,"E111")])]})});
            var Q80;
            Q80=makeQuery(id+"F5.boolean.opBoolean","COPY",EDGE,{"derivedFrom":makeQuery(id+"F5.opExtrude","SWEPT_EDGE",EDGE,{"disambiguationData":[OSD([sQuery(id+"F4.wireOp",EDGE,"E139.left"),sQuery(id+"F4.wireOp",EDGE,"E139.bottom")])]})});
            var Q81;
            Q81=makeQuery(id+"F5.boolean.opBoolean","COPY",EDGE,{"derivedFrom":makeQuery(id+"F5.opExtrude","SWEPT_EDGE",EDGE,{"disambiguationData":[OSD([sQuery(id+"F4.wireOp",EDGE,"E85"),sQuery(id+"F4.wireOp",EDGE,"E80.top")])]})});
            var Q82;
            Q82=makeQuery(id+"F5.boolean.opBoolean","COPY",EDGE,{"derivedFrom":makeQuery(id+"F5.opExtrude","SWEPT_EDGE",EDGE,{"disambiguationData":[OSD([sQuery(id+"F4.wireOp",EDGE,"E99"),sQuery(id+"F4.wireOp",EDGE,"E106.top")])]})});
            var Q83;
            Q83=makeQuery(id+"F5.boolean.opBoolean","COPY",EDGE,{"derivedFrom":makeQuery(id+"F5.opExtrude","SWEPT_EDGE",EDGE,{"disambiguationData":[OSD([sQuery(id+"F4.wireOp",EDGE,"E90"),sQuery(id+"F4.wireOp",EDGE,"E87.top")])]})});
            var Q84;
            Q84=makeQuery(id+"F5.boolean.opBoolean","COPY",EDGE,{"derivedFrom":makeQuery(id+"F5.opExtrude","SWEPT_EDGE",EDGE,{"disambiguationData":[OSD([sQuery(id+"F4.wireOp",EDGE,"E140.left"),sQuery(id+"F4.wireOp",EDGE,"E140.bottom")])]})});
            var Q85;
            Q85=makeQuery(id+"F5.boolean.opBoolean","COPY",EDGE,{"derivedFrom":makeQuery(id+"F5.opExtrude","SWEPT_EDGE",EDGE,{"disambiguationData":[OSD([sQuery(id+"F4.wireOp",EDGE,"E136.left"),sQuery(id+"F4.wireOp",EDGE,"E136.bottom")])]})});
            var Q86;
            Q86=makeQuery(id+"F5.boolean.opBoolean","COPY",EDGE,{"derivedFrom":makeQuery(id+"F5.opExtrude","SWEPT_EDGE",EDGE,{"disambiguationData":[OSD([sQuery(id+"F4.wireOp",EDGE,"E135.left"),sQuery(id+"F4.wireOp",EDGE,"E135.bottom")])]})});
            var Q87;
            Q87=makeQuery(id+"F5.boolean.opBoolean","COPY",EDGE,{"derivedFrom":makeQuery(id+"F5.opExtrude","SWEPT_EDGE",EDGE,{"disambiguationData":[OSD([sQuery(id+"F4.wireOp",EDGE,"E95.top"),sQuery(id+"F4.wireOp",EDGE,"E102")])]})});
            var Q88;
            Q88=makeQuery(id+"F5.boolean.opBoolean","COPY",EDGE,{"derivedFrom":makeQuery(id+"F5.opExtrude","SWEPT_EDGE",EDGE,{"disambiguationData":[OSD([sQuery(id+"F4.wireOp",EDGE,"E75"),sQuery(id+"F4.wireOp",EDGE,"E76.top")])]})});
            var Q89;
            Q89=makeQuery(id+"F5.boolean.opBoolean","COPY",EDGE,{"derivedFrom":makeQuery(id+"F5.opExtrude","SWEPT_EDGE",EDGE,{"disambiguationData":[OSD([sQuery(id+"F4.wireOp",EDGE,"E77"),sQuery(id+"F4.wireOp",EDGE,"E79.top")])]})});
            var Q90;
            Q90=makeQuery(id+"F5.boolean.opBoolean","COPY",EDGE,{"derivedFrom":makeQuery(id+"F5.opExtrude","SWEPT_EDGE",EDGE,{"disambiguationData":[OSD([sQuery(id+"F4.wireOp",EDGE,"E105"),sQuery(id+"F4.wireOp",EDGE,"E110.top")])]})});
            var Q91;
            Q91=makeQuery(id+"F5.boolean.opBoolean","COPY",EDGE,{"derivedFrom":makeQuery(id+"F5.opExtrude","SWEPT_EDGE",EDGE,{"disambiguationData":[OSD([sQuery(id+"F4.wireOp",EDGE,"E134.left"),sQuery(id+"F4.wireOp",EDGE,"E134.bottom")])]})});
            var Q92;
            Q92=makeQuery(id+"F5.boolean.opBoolean","COPY",EDGE,{"derivedFrom":makeQuery(id+"F5.opExtrude","SWEPT_EDGE",EDGE,{"disambiguationData":[OSD([sQuery(id+"F4.wireOp",EDGE,"E72"),sQuery(id+"F4.wireOp",EDGE,"E73.top")])]})});
            var Q93;
            Q93=makeQuery(id+"F5.boolean.opBoolean","COPY",EDGE,{"derivedFrom":makeQuery(id+"F5.opExtrude","SWEPT_EDGE",EDGE,{"disambiguationData":[OSD([sQuery(id+"F4.wireOp",EDGE,"E97.top"),sQuery(id+"F4.wireOp",EDGE,"E107")])]})});
            var Q94;
            Q94=makeQuery(id+"F5.boolean.opBoolean","COPY",EDGE,{"derivedFrom":makeQuery(id+"F5.opExtrude","SWEPT_EDGE",EDGE,{"disambiguationData":[OSD([sQuery(id+"F4.wireOp",EDGE,"E133.bottom"),sQuery(id+"F4.wireOp",EDGE,"E133.left")])]})});
            var Q95;
            Q95=makeQuery(id+"F5.boolean.opBoolean","COPY",EDGE,{"derivedFrom":makeQuery(id+"F5.opExtrude","SWEPT_EDGE",EDGE,{"disambiguationData":[OSD([sQuery(id+"F4.wireOp",EDGE,"E98.top"),sQuery(id+"F4.wireOp",EDGE,"E100")])]})});
            var Q96;
            Q96=makeQuery(id+"F5.boolean.opBoolean","COPY",EDGE,{"derivedFrom":makeQuery(id+"F5.opExtrude","SWEPT_EDGE",EDGE,{"disambiguationData":[OSD([sQuery(id+"F4.wireOp",EDGE,"E125.top"),sQuery(id+"F4.wireOp",EDGE,"E127")])]})});
            var Q97;
            Q97=makeQuery(id+"F5.boolean.opBoolean","COPY",EDGE,{"derivedFrom":makeQuery(id+"F5.opExtrude","SWEPT_EDGE",EDGE,{"disambiguationData":[OSD([sQuery(id+"F4.wireOp",EDGE,"E68.top"),sQuery(id+"F4.wireOp",EDGE,"E70")])]})});
            var Q98;
            Q98=makeQuery(id+"F5.boolean.opBoolean","COPY",EDGE,{"derivedFrom":makeQuery(id+"F5.opExtrude","SWEPT_EDGE",EDGE,{"disambiguationData":[OSD([sQuery(id+"F4.wireOp",EDGE,"E96.top"),sQuery(id+"F4.wireOp",EDGE,"E101")])]})});
            var Q99;
            Q99=makeQuery(id+"F5.boolean.opBoolean","COPY",EDGE,{"derivedFrom":makeQuery(id+"F5.opExtrude","SWEPT_EDGE",EDGE,{"disambiguationData":[OSD([sQuery(id+"F4.wireOp",EDGE,"E84.top"),sQuery(id+"F4.wireOp",EDGE,"E84.left")])]})});
            var Q100;
            Q100=makeQuery(id+"F5.boolean.opBoolean","COPY",EDGE,{"derivedFrom":makeQuery(id+"F5.opExtrude","SWEPT_EDGE",EDGE,{"disambiguationData":[OSD([sQuery(id+"F4.wireOp",EDGE,"E103.top"),sQuery(id+"F4.wireOp",EDGE,"E103.left")])]})});
            var Q101;
            Q101=makeQuery(id+"F5.boolean.opBoolean","COPY",EDGE,{"derivedFrom":makeQuery(id+"F5.opExtrude","SWEPT_EDGE",EDGE,{"disambiguationData":[OSD([sQuery(id+"F4.wireOp",EDGE,"E137.right"),sQuery(id+"F4.wireOp",EDGE,"E137.bottom")])]})});
            var Q102;
            Q102=makeQuery(id+"F5.boolean.opBoolean","COPY",EDGE,{"derivedFrom":makeQuery(id+"F5.opExtrude","SWEPT_EDGE",EDGE,{"disambiguationData":[OSD([sQuery(id+"F4.wireOp",EDGE,"E138.right"),sQuery(id+"F4.wireOp",EDGE,"E138.bottom")])]})});
            var Q103;
            Q103=makeQuery(id+"F5.boolean.opBoolean","COPY",EDGE,{"derivedFrom":makeQuery(id+"F5.opExtrude","SWEPT_EDGE",EDGE,{"disambiguationData":[OSD([sQuery(id+"F4.wireOp",EDGE,"E104.left"),sQuery(id+"F4.wireOp",EDGE,"E104.top")])]})});
            var Q104;
            Q104=makeQuery(id+"F5.boolean.opBoolean","COPY",EDGE,{"derivedFrom":makeQuery(id+"F5.opExtrude","SWEPT_EDGE",EDGE,{"disambiguationData":[OSD([sQuery(id+"F4.wireOp",EDGE,"E87.left"),sQuery(id+"F4.wireOp",EDGE,"E87.top")])]})});
            var Q105;
            Q105=makeQuery(id+"F5.boolean.opBoolean","COPY",EDGE,{"derivedFrom":makeQuery(id+"F5.opExtrude","SWEPT_EDGE",EDGE,{"disambiguationData":[OSD([sQuery(id+"F4.wireOp",EDGE,"E80.top"),sQuery(id+"F4.wireOp",EDGE,"E80.left")])]})});
            var Q106;
            Q106=makeQuery(id+"F5.boolean.opBoolean","COPY",EDGE,{"derivedFrom":makeQuery(id+"F5.opExtrude","SWEPT_EDGE",EDGE,{"disambiguationData":[OSD([sQuery(id+"F4.wireOp",EDGE,"E106.left"),sQuery(id+"F4.wireOp",EDGE,"E106.top")])]})});
            var Q107;
            Q107=makeQuery(id+"F5.boolean.opBoolean","COPY",EDGE,{"derivedFrom":makeQuery(id+"F5.opExtrude","SWEPT_EDGE",EDGE,{"disambiguationData":[OSD([sQuery(id+"F4.wireOp",EDGE,"E139.right"),sQuery(id+"F4.wireOp",EDGE,"E139.bottom")])]})});
            var Q108;
            Q108=makeQuery(id+"F5.boolean.opBoolean","COPY",EDGE,{"derivedFrom":makeQuery(id+"F5.opExtrude","SWEPT_EDGE",EDGE,{"disambiguationData":[OSD([sQuery(id+"F4.wireOp",EDGE,"E140.right"),sQuery(id+"F4.wireOp",EDGE,"E140.bottom")])]})});
            var Q109;
            Q109=makeQuery(id+"F5.boolean.opBoolean","COPY",EDGE,{"derivedFrom":makeQuery(id+"F5.opExtrude","SWEPT_EDGE",EDGE,{"disambiguationData":[OSD([sQuery(id+"F4.wireOp",EDGE,"E96.top"),sQuery(id+"F4.wireOp",EDGE,"E96.left")])]})});
            var Q110;
            Q110=makeQuery(id+"F5.boolean.opBoolean","COPY",EDGE,{"derivedFrom":makeQuery(id+"F5.opExtrude","SWEPT_EDGE",EDGE,{"disambiguationData":[OSD([sQuery(id+"F4.wireOp",EDGE,"E76.left"),sQuery(id+"F4.wireOp",EDGE,"E76.top")])]})});
            var Q111;
            Q111=makeQuery(id+"F5.boolean.opBoolean","COPY",EDGE,{"derivedFrom":makeQuery(id+"F5.opExtrude","SWEPT_EDGE",EDGE,{"disambiguationData":[OSD([sQuery(id+"F4.wireOp",EDGE,"E79.left"),sQuery(id+"F4.wireOp",EDGE,"E79.top")])]})});
            var Q112;
            Q112=makeQuery(id+"F5.boolean.opBoolean","COPY",EDGE,{"derivedFrom":makeQuery(id+"F5.opExtrude","SWEPT_EDGE",EDGE,{"disambiguationData":[OSD([sQuery(id+"F4.wireOp",EDGE,"E73.top"),sQuery(id+"F4.wireOp",EDGE,"E73.left")])]})});
            var Q113;
            Q113=makeQuery(id+"F5.boolean.opBoolean","COPY",EDGE,{"derivedFrom":makeQuery(id+"F5.opExtrude","SWEPT_EDGE",EDGE,{"disambiguationData":[OSD([sQuery(id+"F4.wireOp",EDGE,"E68.top"),sQuery(id+"F4.wireOp",EDGE,"E68.left")])]})});
            var Q114;
            Q114=makeQuery(id+"F5.boolean.opBoolean","COPY",EDGE,{"derivedFrom":makeQuery(id+"F5.opExtrude","SWEPT_EDGE",EDGE,{"disambiguationData":[OSD([sQuery(id+"F4.wireOp",EDGE,"E110.top"),sQuery(id+"F4.wireOp",EDGE,"E110.left")])]})});
            var Q115;
            Q115=makeQuery(id+"F5.boolean.opBoolean","COPY",EDGE,{"derivedFrom":makeQuery(id+"F5.opExtrude","SWEPT_EDGE",EDGE,{"disambiguationData":[OSD([sQuery(id+"F4.wireOp",EDGE,"E97.top"),sQuery(id+"F4.wireOp",EDGE,"E97.left")])]})});
            var Q116;
            Q116=makeQuery(id+"F5.boolean.opBoolean","COPY",EDGE,{"derivedFrom":makeQuery(id+"F5.opExtrude","SWEPT_EDGE",EDGE,{"disambiguationData":[OSD([sQuery(id+"F4.wireOp",EDGE,"E125.top"),sQuery(id+"F4.wireOp",EDGE,"E125.left")])]})});
            var Q117;
            Q117=makeQuery(id+"F5.boolean.opBoolean","COPY",EDGE,{"derivedFrom":makeQuery(id+"F5.opExtrude","SWEPT_EDGE",EDGE,{"disambiguationData":[OSD([sQuery(id+"F4.wireOp",EDGE,"E98.left"),sQuery(id+"F4.wireOp",EDGE,"E98.top")])]})});
            var Q118;
            Q118=makeQuery(id+"F5.boolean.opBoolean","COPY",EDGE,{"derivedFrom":makeQuery(id+"F5.opExtrude","SWEPT_EDGE",EDGE,{"disambiguationData":[OSD([sQuery(id+"F4.wireOp",EDGE,"E133.bottom"),sQuery(id+"F4.wireOp",EDGE,"E133.right")])]})});
            var Q119;
            Q119=makeQuery(id+"F5.boolean.opBoolean","COPY",EDGE,{"derivedFrom":makeQuery(id+"F5.opExtrude","SWEPT_EDGE",EDGE,{"disambiguationData":[OSD([sQuery(id+"F4.wireOp",EDGE,"E134.right"),sQuery(id+"F4.wireOp",EDGE,"E134.bottom")])]})});
            var Q120;
            Q120=makeQuery(id+"F5.boolean.opBoolean","COPY",EDGE,{"derivedFrom":makeQuery(id+"F5.opExtrude","SWEPT_EDGE",EDGE,{"disambiguationData":[OSD([sQuery(id+"F4.wireOp",EDGE,"E135.bottom"),sQuery(id+"F4.wireOp",EDGE,"E135.right")])]})});
            var Q121;
            Q121=makeQuery(id+"F5.boolean.opBoolean","COPY",EDGE,{"derivedFrom":makeQuery(id+"F5.opExtrude","SWEPT_EDGE",EDGE,{"disambiguationData":[OSD([sQuery(id+"F4.wireOp",EDGE,"E136.right"),sQuery(id+"F4.wireOp",EDGE,"E136.bottom")])]})});
            var Q122;
            Q122=makeQuery(id+"F5.boolean.opBoolean","COPY",EDGE,{"derivedFrom":makeQuery(id+"F5.opExtrude","SWEPT_EDGE",EDGE,{"disambiguationData":[OSD([sQuery(id+"F4.wireOp",EDGE,"E137.top"),sQuery(id+"F4.wireOp",EDGE,"E137.left")])]})});
            var Q123;
            Q123=makeQuery(id+"F5.boolean.opBoolean","COPY",EDGE,{"derivedFrom":makeQuery(id+"F5.opExtrude","SWEPT_EDGE",EDGE,{"disambiguationData":[OSD([sQuery(id+"F4.wireOp",EDGE,"E108"),sQuery(id+"F4.wireOp",EDGE,"E116.top")])]})});
            var Q124;
            Q124=makeQuery(id+"F5.boolean.opBoolean","COPY",EDGE,{"derivedFrom":makeQuery(id+"F5.opExtrude","SWEPT_EDGE",EDGE,{"disambiguationData":[OSD([sQuery(id+"F4.wireOp",EDGE,"E111"),sQuery(id+"F4.wireOp",EDGE,"E120.top")])]})});
            var Q125;
            Q125=makeQuery(id+"F5.boolean.opBoolean","COPY",EDGE,{"derivedFrom":makeQuery(id+"F5.opExtrude","SWEPT_EDGE",EDGE,{"disambiguationData":[OSD([sQuery(id+"F4.wireOp",EDGE,"E138.left"),sQuery(id+"F4.wireOp",EDGE,"E138.top")])]})});
            var Q126;
            Q126=makeQuery(id+"F5.boolean.opBoolean","COPY",EDGE,{"derivedFrom":makeQuery(id+"F5.opExtrude","SWEPT_EDGE",EDGE,{"disambiguationData":[OSD([sQuery(id+"F4.wireOp",EDGE,"E99"),sQuery(id+"F4.wireOp",EDGE,"E114.top")])]})});
            var Q127;
            Q127=makeQuery(id+"F5.boolean.opBoolean","COPY",EDGE,{"derivedFrom":makeQuery(id+"F5.opExtrude","SWEPT_EDGE",EDGE,{"disambiguationData":[OSD([sQuery(id+"F4.wireOp",EDGE,"E139.left"),sQuery(id+"F4.wireOp",EDGE,"E139.top")])]})});
            var Q128;
            Q128=makeQuery(id+"F5.boolean.opBoolean","COPY",EDGE,{"derivedFrom":makeQuery(id+"F5.opExtrude","SWEPT_EDGE",EDGE,{"disambiguationData":[OSD([sQuery(id+"F4.wireOp",EDGE,"E90"),sQuery(id+"F4.wireOp",EDGE,"E81.top")])]})});
            var Q129;
            Q129=makeQuery(id+"F5.boolean.opBoolean","COPY",EDGE,{"derivedFrom":makeQuery(id+"F5.opExtrude","SWEPT_EDGE",EDGE,{"disambiguationData":[OSD([sQuery(id+"F4.wireOp",EDGE,"E74.top"),sQuery(id+"F4.wireOp",EDGE,"E75")])]})});
            var Q130;
            Q130=makeQuery(id+"F5.boolean.opBoolean","COPY",EDGE,{"derivedFrom":makeQuery(id+"F5.opExtrude","SWEPT_EDGE",EDGE,{"disambiguationData":[OSD([sQuery(id+"F4.wireOp",EDGE,"E77"),sQuery(id+"F4.wireOp",EDGE,"E78.top")])]})});
            var Q131;
            Q131=makeQuery(id+"F5.boolean.opBoolean","COPY",EDGE,{"derivedFrom":makeQuery(id+"F5.opExtrude","SWEPT_EDGE",EDGE,{"disambiguationData":[OSD([sQuery(id+"F4.wireOp",EDGE,"E101"),sQuery(id+"F4.wireOp",EDGE,"E117.top")])]})});
            var Q132;
            Q132=makeQuery(id+"F5.boolean.opBoolean","COPY",EDGE,{"derivedFrom":makeQuery(id+"F5.opExtrude","SWEPT_EDGE",EDGE,{"disambiguationData":[OSD([sQuery(id+"F4.wireOp",EDGE,"E140.left"),sQuery(id+"F4.wireOp",EDGE,"E140.top")])]})});
            var Q133;
            Q133=makeQuery(id+"F5.boolean.opBoolean","COPY",EDGE,{"derivedFrom":makeQuery(id+"F5.opExtrude","SWEPT_EDGE",EDGE,{"disambiguationData":[OSD([sQuery(id+"F4.wireOp",EDGE,"E83.top"),sQuery(id+"F4.wireOp",EDGE,"E85")])]})});
            var Q134;
            Q134=makeQuery(id+"F5.boolean.opBoolean","COPY",EDGE,{"derivedFrom":makeQuery(id+"F5.opExtrude","SWEPT_EDGE",EDGE,{"disambiguationData":[OSD([sQuery(id+"F4.wireOp",EDGE,"E136.left"),sQuery(id+"F4.wireOp",EDGE,"E136.top")])]})});
            var Q135;
            Q135=makeQuery(id+"F5.boolean.opBoolean","COPY",EDGE,{"derivedFrom":makeQuery(id+"F5.opExtrude","SWEPT_EDGE",EDGE,{"disambiguationData":[OSD([sQuery(id+"F4.wireOp",EDGE,"E102"),sQuery(id+"F4.wireOp",EDGE,"E119.top")])]})});
            var Q136;
            Q136=makeQuery(id+"F5.boolean.opBoolean","COPY",EDGE,{"derivedFrom":makeQuery(id+"F5.opExtrude","SWEPT_EDGE",EDGE,{"disambiguationData":[OSD([sQuery(id+"F4.wireOp",EDGE,"E135.left"),sQuery(id+"F4.wireOp",EDGE,"E135.top")])]})});
            var Q137;
            Q137=makeQuery(id+"F5.boolean.opBoolean","COPY",EDGE,{"derivedFrom":makeQuery(id+"F5.opExtrude","SWEPT_EDGE",EDGE,{"disambiguationData":[OSD([sQuery(id+"F4.wireOp",EDGE,"E105"),sQuery(id+"F4.wireOp",EDGE,"E121.top")])]})});
            var Q138;
            Q138=makeQuery(id+"F5.boolean.opBoolean","COPY",EDGE,{"derivedFrom":makeQuery(id+"F5.opExtrude","SWEPT_EDGE",EDGE,{"disambiguationData":[OSD([sQuery(id+"F4.wireOp",EDGE,"E72"),sQuery(id+"F4.wireOp",EDGE,"E71.top")])]})});
            var Q139;
            Q139=makeQuery(id+"F5.boolean.opBoolean","COPY",EDGE,{"derivedFrom":makeQuery(id+"F5.opExtrude","SWEPT_EDGE",EDGE,{"disambiguationData":[OSD([sQuery(id+"F4.wireOp",EDGE,"E69.top"),sQuery(id+"F4.wireOp",EDGE,"E70")])]})});
            var Q140;
            Q140=makeQuery(id+"F5.boolean.opBoolean","COPY",EDGE,{"derivedFrom":makeQuery(id+"F5.opExtrude","SWEPT_EDGE",EDGE,{"disambiguationData":[OSD([sQuery(id+"F4.wireOp",EDGE,"E107"),sQuery(id+"F4.wireOp",EDGE,"E115.top")])]})});
            var Q141;
            Q141=makeQuery(id+"F5.boolean.opBoolean","COPY",EDGE,{"derivedFrom":makeQuery(id+"F5.opExtrude","SWEPT_EDGE",EDGE,{"disambiguationData":[OSD([sQuery(id+"F4.wireOp",EDGE,"E134.left"),sQuery(id+"F4.wireOp",EDGE,"E134.top")])]})});
            var Q142;
            Q142=makeQuery(id+"F5.boolean.opBoolean","COPY",EDGE,{"derivedFrom":makeQuery(id+"F5.opExtrude","SWEPT_EDGE",EDGE,{"disambiguationData":[OSD([sQuery(id+"F4.wireOp",EDGE,"E133.top"),sQuery(id+"F4.wireOp",EDGE,"E133.left")])]})});
            var Q143;
            Q143=makeQuery(id+"F5.boolean.opBoolean","COPY",EDGE,{"derivedFrom":makeQuery(id+"F5.opExtrude","SWEPT_EDGE",EDGE,{"disambiguationData":[OSD([sQuery(id+"F4.wireOp",EDGE,"E100"),sQuery(id+"F4.wireOp",EDGE,"E118.top")])]})});
            var Q144;
            Q144=makeQuery(id+"F5.boolean.opBoolean","COPY",EDGE,{"derivedFrom":makeQuery(id+"F5.opExtrude","SWEPT_EDGE",EDGE,{"disambiguationData":[OSD([sQuery(id+"F4.wireOp",EDGE,"E126.top"),sQuery(id+"F4.wireOp",EDGE,"E127")])]})});
            var Q145;
            Q145=makeQuery(id+"F5.boolean.opBoolean","COPY",EDGE,{"derivedFrom":makeQuery(id+"F5.opExtrude","SWEPT_EDGE",EDGE,{"disambiguationData":[OSD([sQuery(id+"F4.wireOp",EDGE,"E95.left"),sQuery(id+"F4.wireOp",EDGE,"E95.top")])]})});
            var Q146;
            Q146=makeQuery(id+"F5.boolean.opBoolean","COPY",EDGE,{"derivedFrom":makeQuery(id+"F5.opExtrude","SWEPT_EDGE",EDGE,{"disambiguationData":[OSD([sQuery(id+"F4.wireOp",EDGE,"E82.top"),sQuery(id+"F4.wireOp",EDGE,"E89")])]})});
            var Q147;
            Q147=makeQuery(id+"F5.boolean.opBoolean","COPY",EDGE,{"derivedFrom":makeQuery(id+"F5.opExtrude","SWEPT_EDGE",EDGE,{"disambiguationData":[OSD([sQuery(id+"F4.wireOp",EDGE,"E88"),sQuery(id+"F4.wireOp",EDGE,"E91.top")])]})});
            fillet(context, id + "F6", {"entities" : qUnion([Q0, Q1, Q2, Q3, Q4, Q5, Q6, Q7, Q8, Q9, Q10, Q11, Q12, Q13, Q14, Q15, Q16, Q17, Q18, Q19, Q20, Q21, Q22, Q23, Q24, Q25, Q26, Q27, Q28, Q29, Q30, Q31, Q32, Q33, Q34, Q35, Q36, Q37, Q38, Q39, Q40, Q41, Q42, Q43, Q44, Q45, Q46, Q47, Q48, Q49, Q50, Q51, Q52, Q53, Q54, Q55, Q56, Q57, Q58, Q59, Q60, Q61, Q62, Q63, Q64, Q65, Q66, Q67, Q68, Q69, Q70, Q71, Q72, Q73, Q74, Q75, Q76, Q77, Q78, Q79, Q80, Q81, Q82, Q83, Q84, Q85, Q86, Q87, Q88, Q89, Q90, Q91, Q92, Q93, Q94, Q95, Q96, Q97, Q98, Q99, Q100, Q101, Q102, Q103, Q104, Q105, Q106, Q107, Q108, Q109, Q110, Q111, Q112, Q113, Q114, Q115, Q116, Q117, Q118, Q119, Q120, Q121, Q122, Q123, Q124, Q125, Q126, Q127, Q128, Q129, Q130, Q131, Q132, Q133, Q134, Q135, Q136, Q137, Q138, Q139, Q140, Q141, Q142, Q143, Q144, Q145, Q146, Q147]), "radius" : 2 * mm, "tangentPropagation" : true, "allowEdgeOverflow" : false});
        }
    });
